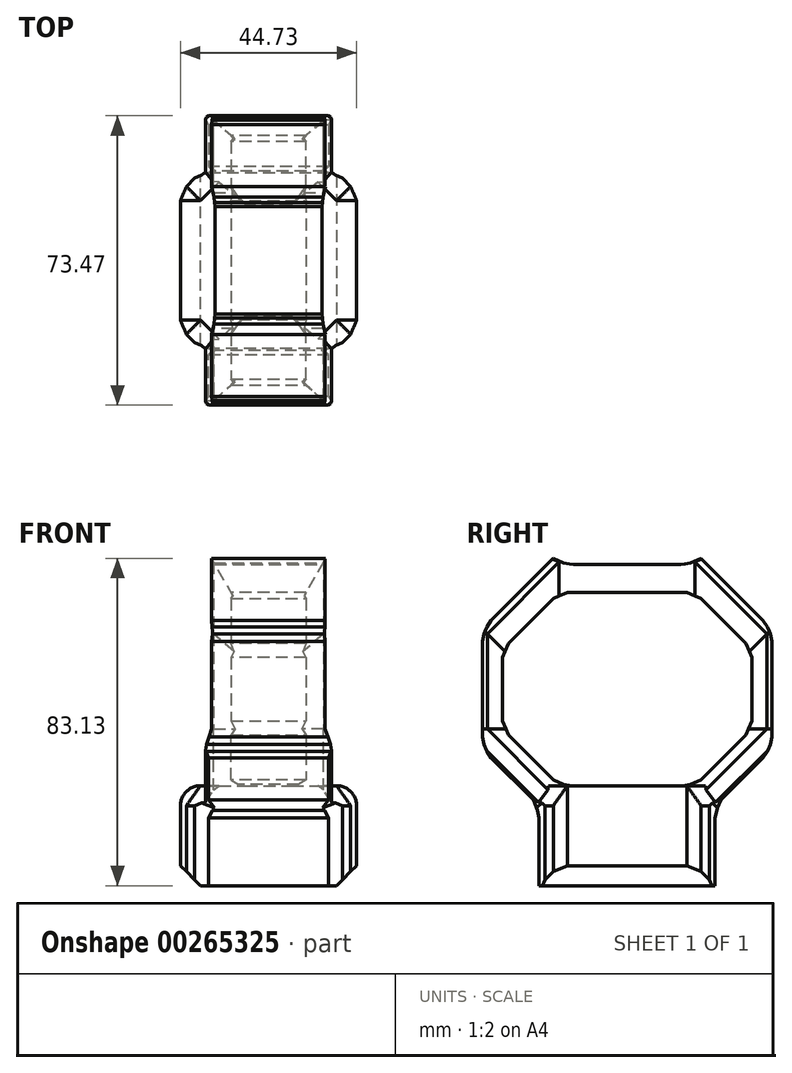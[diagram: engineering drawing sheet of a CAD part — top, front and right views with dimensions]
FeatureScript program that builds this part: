
annotation { "Feature Type Name" : "Feature", "Feature Type Description" : "" }
export const myFeature = defineFeature(function(context is Context, id is Id, definition is map)
    precondition{}
    {
        {
            var Q0;
            Q0=qCreatedBy(makeId("Top.planeOp"),FACE);
            var sketch = newSketch(context, id + "F0", { "sketchPlane" : qUnion([Q0])});
            skLineSegment(sketch, "E0", {"start": v(0, 0) * mm, "end": v(0, 44.73) * mm});
            skLineSegment(sketch, "E1", {"start": v(0, 44.73) * mm, "end": v(-44.73, 44.73) * mm});
            skLineSegment(sketch, "E2", {"start": v(-44.73, 44.73) * mm, "end": v(-44.73, 0) * mm});
            skLineSegment(sketch, "E3", {"start": v(-44.73, 0) * mm, "end": v(0, 0) * mm});
            skSolve(sketch);
        }
        {
            var Q0;
            Q0=makeQuery(id+"F0.imprint","IMPRINT",FACE,{"disambiguationData":[TD([[makeQuery(id+"F0.imprint","IMPRINT",EDGE,{"derivedFrom":sQuery(id+"F0.wireOp",EDGE,"E0")}),1.0]])]});
            extrude(context, id + "F1", {"entities" : qUnion([Q0]), "depth" : 25.4 * mm});
        }
        {
            var Q0;
            Q0=makeQuery(id+"F1.opExtrude","CAP_EDGE",EDGE,{"disambiguationData":[OSD([sQuery(id+"F0.wireOp",EDGE,"E3")])],"isStart":false});
            var Q1;
            Q1=makeQuery(id+"F1.opExtrude","SWEPT_EDGE",EDGE,{"disambiguationData":[OSD([sQuery(id+"F0.wireOp",EDGE,"E2"),sQuery(id+"F0.wireOp",EDGE,"E3")])]});
            var Q2;
            Q2=makeQuery(id+"F1.opExtrude","SWEPT_EDGE",EDGE,{"disambiguationData":[OSD([sQuery(id+"F0.wireOp",EDGE,"E0"),sQuery(id+"F0.wireOp",EDGE,"E3")])]});
            var Q3;
            Q3=makeQuery(id+"F1.opExtrude","CAP_EDGE",EDGE,{"disambiguationData":[OSD([sQuery(id+"F0.wireOp",EDGE,"E1")])],"isStart":false});
            var Q4;
            Q4=makeQuery(id+"F1.opExtrude","SWEPT_EDGE",EDGE,{"disambiguationData":[OSD([sQuery(id+"F0.wireOp",EDGE,"E1"),sQuery(id+"F0.wireOp",EDGE,"E2")])]});
            var Q5;
            Q5=makeQuery(id+"F1.opExtrude","SWEPT_EDGE",EDGE,{"disambiguationData":[OSD([sQuery(id+"F0.wireOp",EDGE,"E0"),sQuery(id+"F0.wireOp",EDGE,"E1")])]});
            chamfer(context, id + "F2", {"entities" : qUnion([Q0, Q1, Q2, Q3, Q4, Q5]), "width" : 5.08 * mm, "tangentPropagation" : true});
        }
        {
            var Q0;
            {var subQ0=sQuery(id+"F0.wireOp",EDGE,"E3");Q0=makeQuery(id+"F2.opChamfer","BLEND_EDGE",EDGE,{"blendedFrom":[makeQuery(id+"F1.opExtrude","SWEPT_EDGE",EDGE,{"disambiguationData":[OSD([sQuery(id+"F0.wireOp",EDGE,"E2"),subQ0])]}),makeQuery(id+"F1.opExtrude","SWEPT_FACE",FACE,{"disambiguationData":[OSD([subQ0])]})],"blendedInto":[makeQuery(id+"F1.opExtrude","SWEPT_FACE",FACE,{"disambiguationData":[OSD([subQ0])]})]});}
            var Q1;
            {var subQ0=sQuery(id+"F0.wireOp",EDGE,"E3");Q1=makeQuery(id+"F2.opChamfer","BLEND_EDGE",EDGE,{"blendedFrom":[makeQuery(id+"F1.opExtrude","SWEPT_EDGE",EDGE,{"disambiguationData":[OSD([sQuery(id+"F0.wireOp",EDGE,"E0"),subQ0])]}),makeQuery(id+"F1.opExtrude","SWEPT_FACE",FACE,{"disambiguationData":[OSD([subQ0])]})],"blendedInto":[makeQuery(id+"F1.opExtrude","SWEPT_FACE",FACE,{"disambiguationData":[OSD([subQ0])]})]});}
            var Q2;
            {var subQ0=sQuery(id+"F0.wireOp",EDGE,"E1");Q2=makeQuery(id+"F2.opChamfer","BLEND_EDGE",EDGE,{"blendedFrom":[makeQuery(id+"F1.opExtrude","SWEPT_EDGE",EDGE,{"disambiguationData":[OSD([sQuery(id+"F0.wireOp",EDGE,"E0"),subQ0])]}),makeQuery(id+"F1.opExtrude","SWEPT_FACE",FACE,{"disambiguationData":[OSD([subQ0])]})],"blendedInto":[makeQuery(id+"F1.opExtrude","SWEPT_FACE",FACE,{"disambiguationData":[OSD([subQ0])]})]});}
            var Q3;
            {var subQ0=sQuery(id+"F0.wireOp",EDGE,"E1");Q3=makeQuery(id+"F2.opChamfer","BLEND_EDGE",EDGE,{"blendedFrom":[makeQuery(id+"F1.opExtrude","SWEPT_EDGE",EDGE,{"disambiguationData":[OSD([subQ0,sQuery(id+"F0.wireOp",EDGE,"E2")])]}),makeQuery(id+"F1.opExtrude","SWEPT_FACE",FACE,{"disambiguationData":[OSD([subQ0])]})],"blendedInto":[makeQuery(id+"F1.opExtrude","SWEPT_FACE",FACE,{"disambiguationData":[OSD([subQ0])]})]});}
            chamfer(context, id + "F3", {"entities" : qUnion([Q0, Q1, Q2, Q3]), "width" : 5.08 * mm, "tangentPropagation" : true});
        }
        {
            var Q0;
            Q0=makeQuery(id+"F2.opChamfer","BLEND_FACE",FACE,{"disambiguationData":[OSD([sQuery(id+"F0.wireOp",EDGE,"E3")])]});
            extrude(context, id + "F4", {"entities" : qUnion([Q0]), "operationType" : NewBodyOperationType.ADD, "depth" : 25.4 * mm});
        }
        {
            var Q0;
            Q0=makeQuery(id+"F2.opChamfer","BLEND_FACE",FACE,{"disambiguationData":[OSD([sQuery(id+"F0.wireOp",EDGE,"E1")])]});
            extrude(context, id + "F5", {"entities" : qUnion([Q0]), "operationType" : NewBodyOperationType.ADD, "depth" : 25.4 * mm});
        }
        {
            var Q0;
            {var subQ0=sQuery(id+"F0.wireOp",EDGE,"E2");var subQ1=sQuery(id+"F0.wireOp",EDGE,"E3");var subQ2=sQuery(id+"F0.wireOp",EDGE,"E1");var subQ3=sQuery(id+"F0.wireOp",EDGE,"E0");Q0=makeQuery(id+"F5.opExtrude","SWEPT_EDGE",EDGE,{"disambiguationData":[OSD([subQ3,subQ2,subQ0,subQ1]),TDD([makeQuery(id+"F2.opChamfer","BLEND_VERTEX",VERTEX,{"blendedFrom":[makeQuery(id+"F1.opExtrude","SWEPT_EDGE",EDGE,{"disambiguationData":[OSD([subQ2,subQ0])]}),makeQuery(id+"F1.opExtrude","CAP_EDGE",EDGE,{"disambiguationData":[OSD([subQ2])],"isStart":false}),makeQuery(id+"F1.opExtrude","CAP_FACE",FACE,{"disambiguationData":[OSD([subQ3,subQ2,subQ0,subQ1])],"isStart":false}),makeQuery(id+"F1.opExtrude","SWEPT_FACE",FACE,{"disambiguationData":[OSD([subQ0])]})],"blendedInto":[makeQuery(id+"F1.opExtrude","CAP_FACE",FACE,{"disambiguationData":[OSD([subQ3,subQ2,subQ0,subQ1])],"isStart":false}),makeQuery(id+"F1.opExtrude","SWEPT_FACE",FACE,{"disambiguationData":[OSD([subQ0])]})]})])]});}
            var Q1;
            {var subQ0=sQuery(id+"F0.wireOp",EDGE,"E3");var subQ1=sQuery(id+"F0.wireOp",EDGE,"E2");var subQ2=sQuery(id+"F0.wireOp",EDGE,"E1");var subQ3=sQuery(id+"F0.wireOp",EDGE,"E0");Q1=makeQuery(id+"F5.opExtrude","SWEPT_EDGE",EDGE,{"disambiguationData":[OSD([subQ3,subQ2,subQ1,subQ0]),TDD([makeQuery(id+"F2.opChamfer","BLEND_VERTEX",VERTEX,{"blendedFrom":[makeQuery(id+"F1.opExtrude","SWEPT_EDGE",EDGE,{"disambiguationData":[OSD([subQ3,subQ2])]}),makeQuery(id+"F1.opExtrude","CAP_EDGE",EDGE,{"disambiguationData":[OSD([subQ2])],"isStart":false}),makeQuery(id+"F1.opExtrude","SWEPT_FACE",FACE,{"disambiguationData":[OSD([subQ3])]}),makeQuery(id+"F1.opExtrude","CAP_FACE",FACE,{"disambiguationData":[OSD([subQ3,subQ2,subQ1,subQ0])],"isStart":false})],"blendedInto":[makeQuery(id+"F1.opExtrude","SWEPT_FACE",FACE,{"disambiguationData":[OSD([subQ3])]}),makeQuery(id+"F1.opExtrude","CAP_FACE",FACE,{"disambiguationData":[OSD([subQ3,subQ2,subQ1,subQ0])],"isStart":false})]})])]});}
            var Q2;
            {var subQ0=sQuery(id+"F0.wireOp",EDGE,"E3");var subQ1=sQuery(id+"F0.wireOp",EDGE,"E2");var subQ2=sQuery(id+"F0.wireOp",EDGE,"E1");var subQ3=sQuery(id+"F0.wireOp",EDGE,"E0");Q2=makeQuery(id+"F4.opExtrude","SWEPT_EDGE",EDGE,{"disambiguationData":[OSD([subQ3,subQ2,subQ1,subQ0]),TDD([makeQuery(id+"F2.opChamfer","BLEND_VERTEX",VERTEX,{"blendedFrom":[makeQuery(id+"F1.opExtrude","SWEPT_EDGE",EDGE,{"disambiguationData":[OSD([subQ3,subQ0])]}),makeQuery(id+"F1.opExtrude","CAP_EDGE",EDGE,{"disambiguationData":[OSD([subQ0])],"isStart":false}),makeQuery(id+"F1.opExtrude","SWEPT_FACE",FACE,{"disambiguationData":[OSD([subQ3])]}),makeQuery(id+"F1.opExtrude","CAP_FACE",FACE,{"disambiguationData":[OSD([subQ3,subQ2,subQ1,subQ0])],"isStart":false})],"blendedInto":[makeQuery(id+"F1.opExtrude","SWEPT_FACE",FACE,{"disambiguationData":[OSD([subQ3])]}),makeQuery(id+"F1.opExtrude","CAP_FACE",FACE,{"disambiguationData":[OSD([subQ3,subQ2,subQ1,subQ0])],"isStart":false})]})])]});}
            var Q3;
            {var subQ0=sQuery(id+"F0.wireOp",EDGE,"E2");var subQ1=sQuery(id+"F0.wireOp",EDGE,"E3");var subQ2=sQuery(id+"F0.wireOp",EDGE,"E1");var subQ3=sQuery(id+"F0.wireOp",EDGE,"E0");Q3=makeQuery(id+"F4.opExtrude","SWEPT_EDGE",EDGE,{"disambiguationData":[OSD([subQ3,subQ2,subQ0,subQ1]),TDD([makeQuery(id+"F2.opChamfer","BLEND_VERTEX",VERTEX,{"blendedFrom":[makeQuery(id+"F1.opExtrude","SWEPT_EDGE",EDGE,{"disambiguationData":[OSD([subQ0,subQ1])]}),makeQuery(id+"F1.opExtrude","CAP_EDGE",EDGE,{"disambiguationData":[OSD([subQ1])],"isStart":false}),makeQuery(id+"F1.opExtrude","CAP_FACE",FACE,{"disambiguationData":[OSD([subQ3,subQ2,subQ0,subQ1])],"isStart":false}),makeQuery(id+"F1.opExtrude","SWEPT_FACE",FACE,{"disambiguationData":[OSD([subQ0])]})],"blendedInto":[makeQuery(id+"F1.opExtrude","CAP_FACE",FACE,{"disambiguationData":[OSD([subQ3,subQ2,subQ0,subQ1])],"isStart":false}),makeQuery(id+"F1.opExtrude","SWEPT_FACE",FACE,{"disambiguationData":[OSD([subQ0])]})]})])]});}
            chamfer(context, id + "F6", {"entities" : qUnion([Q0, Q1, Q2, Q3]), "width" : 5.08 * mm, "tangentPropagation" : true});
        }
        {
            var Q0;
            {var subQ0=sQuery(id+"F0.wireOp",EDGE,"E3");var subQ1=sQuery(id+"F0.wireOp",EDGE,"E2");var subQ2=sQuery(id+"F0.wireOp",EDGE,"E1");var subQ3=sQuery(id+"F0.wireOp",EDGE,"E0");Q0=makeQuery(id+"F6.opChamfer","BLEND_EDGE",EDGE,{"blendedFrom":[makeQuery(id+"F5.opExtrude","SWEPT_EDGE",EDGE,{"disambiguationData":[OSD([subQ3,subQ2,subQ1,subQ0]),TDD([makeQuery(id+"F2.opChamfer","BLEND_VERTEX",VERTEX,{"blendedFrom":[makeQuery(id+"F1.opExtrude","SWEPT_EDGE",EDGE,{"disambiguationData":[OSD([subQ3,subQ2])]}),makeQuery(id+"F1.opExtrude","CAP_EDGE",EDGE,{"disambiguationData":[OSD([subQ2])],"isStart":false}),makeQuery(id+"F1.opExtrude","SWEPT_FACE",FACE,{"disambiguationData":[OSD([subQ3])]}),makeQuery(id+"F1.opExtrude","CAP_FACE",FACE,{"disambiguationData":[OSD([subQ3,subQ2,subQ1,subQ0])],"isStart":false})],"blendedInto":[makeQuery(id+"F1.opExtrude","SWEPT_FACE",FACE,{"disambiguationData":[OSD([subQ3])]}),makeQuery(id+"F1.opExtrude","CAP_FACE",FACE,{"disambiguationData":[OSD([subQ3,subQ2,subQ1,subQ0])],"isStart":false})]})])]}),makeQuery(id+"F5.opExtrude","SWEPT_FACE",FACE,{"disambiguationData":[OSD([subQ3,subQ2,subQ1,subQ0])]})],"blendedInto":[makeQuery(id+"F5.opExtrude","SWEPT_FACE",FACE,{"disambiguationData":[OSD([subQ3,subQ2,subQ1,subQ0])]})]});}
            var Q1;
            {var subQ0=sQuery(id+"F0.wireOp",EDGE,"E3");var subQ1=sQuery(id+"F0.wireOp",EDGE,"E2");var subQ2=sQuery(id+"F0.wireOp",EDGE,"E1");var subQ3=sQuery(id+"F0.wireOp",EDGE,"E0");Q1=makeQuery(id+"F6.opChamfer","BLEND_EDGE",EDGE,{"blendedFrom":[makeQuery(id+"F5.opExtrude","SWEPT_EDGE",EDGE,{"disambiguationData":[OSD([subQ3,subQ2,subQ1,subQ0]),TDD([makeQuery(id+"F2.opChamfer","BLEND_VERTEX",VERTEX,{"blendedFrom":[makeQuery(id+"F1.opExtrude","SWEPT_EDGE",EDGE,{"disambiguationData":[OSD([subQ2,subQ1])]}),makeQuery(id+"F1.opExtrude","CAP_EDGE",EDGE,{"disambiguationData":[OSD([subQ2])],"isStart":false}),makeQuery(id+"F1.opExtrude","CAP_FACE",FACE,{"disambiguationData":[OSD([subQ3,subQ2,subQ1,subQ0])],"isStart":false}),makeQuery(id+"F1.opExtrude","SWEPT_FACE",FACE,{"disambiguationData":[OSD([subQ1])]})],"blendedInto":[makeQuery(id+"F1.opExtrude","CAP_FACE",FACE,{"disambiguationData":[OSD([subQ3,subQ2,subQ1,subQ0])],"isStart":false}),makeQuery(id+"F1.opExtrude","SWEPT_FACE",FACE,{"disambiguationData":[OSD([subQ1])]})]})])]}),makeQuery(id+"F5.opExtrude","SWEPT_FACE",FACE,{"disambiguationData":[OSD([subQ3,subQ2,subQ1,subQ0])]})],"blendedInto":[makeQuery(id+"F5.opExtrude","SWEPT_FACE",FACE,{"disambiguationData":[OSD([subQ3,subQ2,subQ1,subQ0])]})]});}
            var Q2;
            {var subQ0=sQuery(id+"F0.wireOp",EDGE,"E3");var subQ1=sQuery(id+"F0.wireOp",EDGE,"E2");var subQ2=sQuery(id+"F0.wireOp",EDGE,"E1");var subQ3=sQuery(id+"F0.wireOp",EDGE,"E0");Q2=makeQuery(id+"F6.opChamfer","BLEND_EDGE",EDGE,{"blendedFrom":[makeQuery(id+"F4.opExtrude","SWEPT_EDGE",EDGE,{"disambiguationData":[OSD([subQ3,subQ2,subQ1,subQ0]),TDD([makeQuery(id+"F2.opChamfer","BLEND_VERTEX",VERTEX,{"blendedFrom":[makeQuery(id+"F1.opExtrude","SWEPT_EDGE",EDGE,{"disambiguationData":[OSD([subQ3,subQ0])]}),makeQuery(id+"F1.opExtrude","CAP_EDGE",EDGE,{"disambiguationData":[OSD([subQ0])],"isStart":false}),makeQuery(id+"F1.opExtrude","SWEPT_FACE",FACE,{"disambiguationData":[OSD([subQ3])]}),makeQuery(id+"F1.opExtrude","CAP_FACE",FACE,{"disambiguationData":[OSD([subQ3,subQ2,subQ1,subQ0])],"isStart":false})],"blendedInto":[makeQuery(id+"F1.opExtrude","SWEPT_FACE",FACE,{"disambiguationData":[OSD([subQ3])]}),makeQuery(id+"F1.opExtrude","CAP_FACE",FACE,{"disambiguationData":[OSD([subQ3,subQ2,subQ1,subQ0])],"isStart":false})]})])]}),makeQuery(id+"F4.opExtrude","SWEPT_FACE",FACE,{"disambiguationData":[OSD([subQ3,subQ2,subQ1,subQ0])]})],"blendedInto":[makeQuery(id+"F4.opExtrude","SWEPT_FACE",FACE,{"disambiguationData":[OSD([subQ3,subQ2,subQ1,subQ0])]})]});}
            var Q3;
            {var subQ0=sQuery(id+"F0.wireOp",EDGE,"E3");var subQ1=sQuery(id+"F0.wireOp",EDGE,"E2");var subQ2=sQuery(id+"F0.wireOp",EDGE,"E1");var subQ3=sQuery(id+"F0.wireOp",EDGE,"E0");Q3=makeQuery(id+"F6.opChamfer","BLEND_EDGE",EDGE,{"blendedFrom":[makeQuery(id+"F4.opExtrude","SWEPT_EDGE",EDGE,{"disambiguationData":[OSD([subQ3,subQ2,subQ1,subQ0]),TDD([makeQuery(id+"F2.opChamfer","BLEND_VERTEX",VERTEX,{"blendedFrom":[makeQuery(id+"F1.opExtrude","SWEPT_EDGE",EDGE,{"disambiguationData":[OSD([subQ1,subQ0])]}),makeQuery(id+"F1.opExtrude","CAP_EDGE",EDGE,{"disambiguationData":[OSD([subQ0])],"isStart":false}),makeQuery(id+"F1.opExtrude","CAP_FACE",FACE,{"disambiguationData":[OSD([subQ3,subQ2,subQ1,subQ0])],"isStart":false}),makeQuery(id+"F1.opExtrude","SWEPT_FACE",FACE,{"disambiguationData":[OSD([subQ1])]})],"blendedInto":[makeQuery(id+"F1.opExtrude","CAP_FACE",FACE,{"disambiguationData":[OSD([subQ3,subQ2,subQ1,subQ0])],"isStart":false}),makeQuery(id+"F1.opExtrude","SWEPT_FACE",FACE,{"disambiguationData":[OSD([subQ1])]})]})])]}),makeQuery(id+"F4.opExtrude","SWEPT_FACE",FACE,{"disambiguationData":[OSD([subQ3,subQ2,subQ1,subQ0])]})],"blendedInto":[makeQuery(id+"F4.opExtrude","SWEPT_FACE",FACE,{"disambiguationData":[OSD([subQ3,subQ2,subQ1,subQ0])]})]});}
            chamfer(context, id + "F7", {"entities" : qUnion([Q0, Q1, Q2, Q3]), "width" : 5.08 * mm, "tangentPropagation" : true});
        }
        {
            var Q0;
            {var subQ0=sQuery(id+"F0.wireOp",EDGE,"E3");var subQ1=sQuery(id+"F0.wireOp",EDGE,"E2");var subQ2=sQuery(id+"F0.wireOp",EDGE,"E1");var subQ3=sQuery(id+"F0.wireOp",EDGE,"E0");Q0=makeQuery(id+"F5.boolean.opBoolean","MERGE",EDGE,{"derivedFrom":[makeQuery(id+"F2.opChamfer","BLEND_EDGE",EDGE,{"blendedFrom":[makeQuery(id+"F1.opExtrude","CAP_EDGE",EDGE,{"disambiguationData":[OSD([subQ2])],"isStart":false}),makeQuery(id+"F1.opExtrude","CAP_FACE",FACE,{"disambiguationData":[OSD([subQ3,subQ2,subQ1,subQ0])],"isStart":false})],"blendedInto":[makeQuery(id+"F1.opExtrude","CAP_FACE",FACE,{"disambiguationData":[OSD([subQ3,subQ2,subQ1,subQ0])],"isStart":false})]}),makeQuery(id+"F5.opExtrude","CAP_EDGE",EDGE,{"disambiguationData":[OSD([subQ3,subQ2,subQ1,subQ0])],"isStart":true})]});}
            var Q1;
            {var subQ0=sQuery(id+"F0.wireOp",EDGE,"E3");var subQ1=sQuery(id+"F0.wireOp",EDGE,"E2");var subQ2=sQuery(id+"F0.wireOp",EDGE,"E1");var subQ3=sQuery(id+"F0.wireOp",EDGE,"E0");Q1=makeQuery(id+"F4.boolean.opBoolean","MERGE",EDGE,{"derivedFrom":[makeQuery(id+"F2.opChamfer","BLEND_EDGE",EDGE,{"blendedFrom":[makeQuery(id+"F1.opExtrude","CAP_EDGE",EDGE,{"disambiguationData":[OSD([subQ0])],"isStart":false}),makeQuery(id+"F1.opExtrude","CAP_FACE",FACE,{"disambiguationData":[OSD([subQ3,subQ2,subQ1,subQ0])],"isStart":false})],"blendedInto":[makeQuery(id+"F1.opExtrude","CAP_FACE",FACE,{"disambiguationData":[OSD([subQ3,subQ2,subQ1,subQ0])],"isStart":false})]}),makeQuery(id+"F4.opExtrude","CAP_EDGE",EDGE,{"disambiguationData":[OSD([subQ3,subQ2,subQ1,subQ0])],"isStart":true})]});}
            chamfer(context, id + "F8", {"entities" : qUnion([Q0, Q1]), "width" : 5.08 * mm, "tangentPropagation" : true});
        }
        {
            var Q0;
            Q0=makeQuery(id+"F5.opExtrude","CAP_EDGE",EDGE,{"disambiguationData":[OSD([sQuery(id+"F0.wireOp",EDGE,"E0"),sQuery(id+"F0.wireOp",EDGE,"E1"),sQuery(id+"F0.wireOp",EDGE,"E2"),sQuery(id+"F0.wireOp",EDGE,"E3")])],"isStart":false});
            chamfer(context, id + "F9", {"entities" : qUnion([Q0]), "width" : 5.08 * mm, "tangentPropagation" : true});
        }
        {
            var Q0;
            Q0=makeQuery(id+"F5.opExtrude","CAP_EDGE",EDGE,{"disambiguationData":[OSD([sQuery(id+"F0.wireOp",EDGE,"E1")])],"isStart":false});
            var Q1;
            Q1=makeQuery(id+"F4.opExtrude","CAP_EDGE",EDGE,{"disambiguationData":[OSD([sQuery(id+"F0.wireOp",EDGE,"E0"),sQuery(id+"F0.wireOp",EDGE,"E1"),sQuery(id+"F0.wireOp",EDGE,"E2"),sQuery(id+"F0.wireOp",EDGE,"E3")])],"isStart":false});
            chamfer(context, id + "F10", {"entities" : qUnion([Q0, Q1]), "width" : 5.08 * mm, "tangentPropagation" : true});
        }
        {
            var Q0;
            Q0=makeQuery(id+"F4.opExtrude","CAP_EDGE",EDGE,{"disambiguationData":[OSD([sQuery(id+"F0.wireOp",EDGE,"E3")])],"isStart":false});
            chamfer(context, id + "F11", {"entities" : qUnion([Q0]), "width" : 5.08 * mm, "tangentPropagation" : true});
        }
        {
            var Q0;
            Q0=makeQuery(id+"F9.opChamfer","BLEND_FACE",FACE,{"disambiguationData":[OSD([sQuery(id+"F0.wireOp",EDGE,"E0"),sQuery(id+"F0.wireOp",EDGE,"E1"),sQuery(id+"F0.wireOp",EDGE,"E2"),sQuery(id+"F0.wireOp",EDGE,"E3")])]});
            extrude(context, id + "F12", {"entities" : qUnion([Q0]), "operationType" : NewBodyOperationType.ADD, "depth" : 25.4 * mm});
        }
        {
            var Q0;
            Q0=makeQuery(id+"F10.opChamfer","BLEND_FACE",FACE,{"disambiguationData":[OSD([sQuery(id+"F0.wireOp",EDGE,"E0"),sQuery(id+"F0.wireOp",EDGE,"E1"),sQuery(id+"F0.wireOp",EDGE,"E2"),sQuery(id+"F0.wireOp",EDGE,"E3")])]});
            extrude(context, id + "F13", {"entities" : qUnion([Q0]), "operationType" : NewBodyOperationType.ADD, "depth" : 25.4 * mm});
        }
        {
            var Q0;
            {var subQ0=sQuery(id+"F0.wireOp",EDGE,"E3");var subQ1=sQuery(id+"F0.wireOp",EDGE,"E2");var subQ2=sQuery(id+"F0.wireOp",EDGE,"E1");var subQ3=sQuery(id+"F0.wireOp",EDGE,"E0");Q0=makeQuery(id+"F12.opExtrude","CAP_EDGE",EDGE,{"disambiguationData":[OSD([subQ3,subQ2,subQ1,subQ0]),TDD([makeQuery(id+"F9.opChamfer","BLEND_EDGE",EDGE,{"blendedFrom":[makeQuery(id+"F5.opExtrude","CAP_EDGE",EDGE,{"disambiguationData":[OSD([subQ3,subQ2,subQ1,subQ0])],"isStart":false}),makeQuery(id+"F5.opExtrude","SWEPT_FACE",FACE,{"disambiguationData":[OSD([subQ3,subQ2,subQ1,subQ0])]})],"blendedInto":[makeQuery(id+"F5.opExtrude","SWEPT_FACE",FACE,{"disambiguationData":[OSD([subQ3,subQ2,subQ1,subQ0])]})]})])],"isStart":false});}
            var Q1;
            {var subQ0=sQuery(id+"F0.wireOp",EDGE,"E3");var subQ1=sQuery(id+"F0.wireOp",EDGE,"E2");var subQ2=sQuery(id+"F0.wireOp",EDGE,"E1");var subQ3=sQuery(id+"F0.wireOp",EDGE,"E0");Q1=makeQuery(id+"F13.opExtrude","CAP_EDGE",EDGE,{"disambiguationData":[OSD([subQ3,subQ2,subQ1,subQ0]),TDD([makeQuery(id+"F10.opChamfer","BLEND_EDGE",EDGE,{"blendedFrom":[makeQuery(id+"F4.opExtrude","CAP_EDGE",EDGE,{"disambiguationData":[OSD([subQ3,subQ2,subQ1,subQ0])],"isStart":false}),makeQuery(id+"F4.opExtrude","SWEPT_FACE",FACE,{"disambiguationData":[OSD([subQ3,subQ2,subQ1,subQ0])]})],"blendedInto":[makeQuery(id+"F4.opExtrude","SWEPT_FACE",FACE,{"disambiguationData":[OSD([subQ3,subQ2,subQ1,subQ0])]})]})])],"isStart":false});}
            chamfer(context, id + "F14", {"entities" : qUnion([Q0, Q1]), "width" : 5.08 * mm, "tangentPropagation" : true});
        }
        {
            var Q0;
            {var subQ0=sQuery(id+"F0.wireOp",EDGE,"E3");var subQ1=sQuery(id+"F0.wireOp",EDGE,"E2");var subQ2=sQuery(id+"F0.wireOp",EDGE,"E1");var subQ3=sQuery(id+"F0.wireOp",EDGE,"E0");Q0=makeQuery(id+"F14.opChamfer","BLEND_FACE",FACE,{"disambiguationData":[OSD([subQ3,subQ2,subQ1,subQ0]),TDD([makeQuery(id+"F13.opExtrude","CAP_EDGE",EDGE,{"disambiguationData":[OSD([subQ3,subQ2,subQ1,subQ0]),TDD([makeQuery(id+"F10.opChamfer","BLEND_EDGE",EDGE,{"blendedFrom":[makeQuery(id+"F4.opExtrude","CAP_EDGE",EDGE,{"disambiguationData":[OSD([subQ3,subQ2,subQ1,subQ0])],"isStart":false}),makeQuery(id+"F4.opExtrude","SWEPT_FACE",FACE,{"disambiguationData":[OSD([subQ3,subQ2,subQ1,subQ0])]})],"blendedInto":[makeQuery(id+"F4.opExtrude","SWEPT_FACE",FACE,{"disambiguationData":[OSD([subQ3,subQ2,subQ1,subQ0])]})]})])],"isStart":false})])]});}
            extrude(context, id + "F15", {"entities" : qUnion([Q0]), "operationType" : NewBodyOperationType.ADD, "depth" : 25.4 * mm});
        }
        {
            var Q0;
            {var subQ0=sQuery(id+"F0.wireOp",EDGE,"E3");var subQ1=sQuery(id+"F0.wireOp",EDGE,"E2");var subQ2=sQuery(id+"F0.wireOp",EDGE,"E1");var subQ3=sQuery(id+"F0.wireOp",EDGE,"E0");Q0=makeQuery(id+"F14.opChamfer","BLEND_FACE",FACE,{"disambiguationData":[OSD([subQ3,subQ2,subQ1,subQ0]),TDD([makeQuery(id+"F12.opExtrude","CAP_EDGE",EDGE,{"disambiguationData":[OSD([subQ3,subQ2,subQ1,subQ0]),TDD([makeQuery(id+"F9.opChamfer","BLEND_EDGE",EDGE,{"blendedFrom":[makeQuery(id+"F5.opExtrude","CAP_EDGE",EDGE,{"disambiguationData":[OSD([subQ3,subQ2,subQ1,subQ0])],"isStart":false}),makeQuery(id+"F5.opExtrude","SWEPT_FACE",FACE,{"disambiguationData":[OSD([subQ3,subQ2,subQ1,subQ0])]})],"blendedInto":[makeQuery(id+"F5.opExtrude","SWEPT_FACE",FACE,{"disambiguationData":[OSD([subQ3,subQ2,subQ1,subQ0])]})]})])],"isStart":false})])]});}
            extrude(context, id + "F16", {"entities" : qUnion([Q0]), "operationType" : NewBodyOperationType.ADD, "depth" : 25.4 * mm});
        }
        {
            var Q0;
            {var subQ0=sQuery(id+"F0.wireOp",EDGE,"E3");var subQ1=sQuery(id+"F0.wireOp",EDGE,"E2");var subQ2=sQuery(id+"F0.wireOp",EDGE,"E1");var subQ3=sQuery(id+"F0.wireOp",EDGE,"E0");var subQ4=makeQuery(id+"F9.opChamfer","BLEND_EDGE",EDGE,{"blendedFrom":[makeQuery(id+"F5.opExtrude","CAP_EDGE",EDGE,{"disambiguationData":[OSD([subQ3,subQ2,subQ1,subQ0])],"isStart":false}),makeQuery(id+"F5.opExtrude","SWEPT_FACE",FACE,{"disambiguationData":[OSD([subQ3,subQ2,subQ1,subQ0])]})],"blendedInto":[makeQuery(id+"F5.opExtrude","SWEPT_FACE",FACE,{"disambiguationData":[OSD([subQ3,subQ2,subQ1,subQ0])]})]});Q0=makeQuery(id+"F16.opExtrude","CAP_EDGE",EDGE,{"disambiguationData":[OSD([subQ3,subQ2,subQ1,subQ0]),TDD([makeQuery(id+"F14.opChamfer","BLEND_EDGE",EDGE,{"blendedFrom":[makeQuery(id+"F12.opExtrude","CAP_EDGE",EDGE,{"disambiguationData":[OSD([subQ3,subQ2,subQ1,subQ0]),TDD([subQ4])],"isStart":false}),makeQuery(id+"F12.opExtrude","SWEPT_FACE",FACE,{"disambiguationData":[OSD([subQ3,subQ2,subQ1,subQ0]),TDD([subQ4])]})],"blendedInto":[makeQuery(id+"F12.opExtrude","SWEPT_FACE",FACE,{"disambiguationData":[OSD([subQ3,subQ2,subQ1,subQ0]),TDD([subQ4])]})]})])],"isStart":false});}
            var Q1;
            {var subQ0=sQuery(id+"F0.wireOp",EDGE,"E3");var subQ1=sQuery(id+"F0.wireOp",EDGE,"E2");var subQ2=sQuery(id+"F0.wireOp",EDGE,"E1");var subQ3=sQuery(id+"F0.wireOp",EDGE,"E0");var subQ4=makeQuery(id+"F10.opChamfer","BLEND_EDGE",EDGE,{"blendedFrom":[makeQuery(id+"F4.opExtrude","CAP_EDGE",EDGE,{"disambiguationData":[OSD([subQ3,subQ2,subQ1,subQ0])],"isStart":false}),makeQuery(id+"F4.opExtrude","SWEPT_FACE",FACE,{"disambiguationData":[OSD([subQ3,subQ2,subQ1,subQ0])]})],"blendedInto":[makeQuery(id+"F4.opExtrude","SWEPT_FACE",FACE,{"disambiguationData":[OSD([subQ3,subQ2,subQ1,subQ0])]})]});Q1=makeQuery(id+"F15.opExtrude","CAP_EDGE",EDGE,{"disambiguationData":[OSD([subQ3,subQ2,subQ1,subQ0]),TDD([makeQuery(id+"F14.opChamfer","BLEND_EDGE",EDGE,{"blendedFrom":[makeQuery(id+"F13.opExtrude","CAP_EDGE",EDGE,{"disambiguationData":[OSD([subQ3,subQ2,subQ1,subQ0]),TDD([subQ4])],"isStart":false}),makeQuery(id+"F13.opExtrude","SWEPT_FACE",FACE,{"disambiguationData":[OSD([subQ3,subQ2,subQ1,subQ0]),TDD([subQ4])]})],"blendedInto":[makeQuery(id+"F13.opExtrude","SWEPT_FACE",FACE,{"disambiguationData":[OSD([subQ3,subQ2,subQ1,subQ0]),TDD([subQ4])]})]})])],"isStart":false});}
            chamfer(context, id + "F17", {"entities" : qUnion([Q0, Q1]), "width" : 5.08 * mm, "tangentPropagation" : true});
        }
        {
            var Q0;
            {var subQ0=sQuery(id+"F0.wireOp",EDGE,"E3");var subQ1=sQuery(id+"F0.wireOp",EDGE,"E2");var subQ2=sQuery(id+"F0.wireOp",EDGE,"E1");var subQ3=sQuery(id+"F0.wireOp",EDGE,"E0");var subQ4=makeQuery(id+"F10.opChamfer","BLEND_EDGE",EDGE,{"blendedFrom":[makeQuery(id+"F4.opExtrude","CAP_EDGE",EDGE,{"disambiguationData":[OSD([subQ3,subQ2,subQ1,subQ0])],"isStart":false}),makeQuery(id+"F4.opExtrude","SWEPT_FACE",FACE,{"disambiguationData":[OSD([subQ3,subQ2,subQ1,subQ0])]})],"blendedInto":[makeQuery(id+"F4.opExtrude","SWEPT_FACE",FACE,{"disambiguationData":[OSD([subQ3,subQ2,subQ1,subQ0])]})]});Q0=makeQuery(id+"F17.opChamfer","BLEND_FACE",FACE,{"disambiguationData":[OSD([subQ3,subQ2,subQ1,subQ0]),TDD([makeQuery(id+"F15.opExtrude","CAP_EDGE",EDGE,{"disambiguationData":[OSD([subQ3,subQ2,subQ1,subQ0]),TDD([makeQuery(id+"F14.opChamfer","BLEND_EDGE",EDGE,{"blendedFrom":[makeQuery(id+"F13.opExtrude","CAP_EDGE",EDGE,{"disambiguationData":[OSD([subQ3,subQ2,subQ1,subQ0]),TDD([subQ4])],"isStart":false}),makeQuery(id+"F13.opExtrude","SWEPT_FACE",FACE,{"disambiguationData":[OSD([subQ3,subQ2,subQ1,subQ0]),TDD([subQ4])]})],"blendedInto":[makeQuery(id+"F13.opExtrude","SWEPT_FACE",FACE,{"disambiguationData":[OSD([subQ3,subQ2,subQ1,subQ0]),TDD([subQ4])]})]})])],"isStart":false})])]});}
            extrude(context, id + "F18", {"entities" : qUnion([Q0]), "operationType" : NewBodyOperationType.ADD, "depth" : 25.4 * mm});
        }
        {
            var Q0;
            {var subQ0=sQuery(id+"F0.wireOp",EDGE,"E3");var subQ1=sQuery(id+"F0.wireOp",EDGE,"E2");var subQ2=sQuery(id+"F0.wireOp",EDGE,"E1");var subQ3=sQuery(id+"F0.wireOp",EDGE,"E0");var subQ4=makeQuery(id+"F9.opChamfer","BLEND_EDGE",EDGE,{"blendedFrom":[makeQuery(id+"F5.opExtrude","CAP_EDGE",EDGE,{"disambiguationData":[OSD([subQ3,subQ2,subQ1,subQ0])],"isStart":false}),makeQuery(id+"F5.opExtrude","SWEPT_FACE",FACE,{"disambiguationData":[OSD([subQ3,subQ2,subQ1,subQ0])]})],"blendedInto":[makeQuery(id+"F5.opExtrude","SWEPT_FACE",FACE,{"disambiguationData":[OSD([subQ3,subQ2,subQ1,subQ0])]})]});Q0=makeQuery(id+"F17.opChamfer","BLEND_FACE",FACE,{"disambiguationData":[OSD([subQ3,subQ2,subQ1,subQ0]),TDD([makeQuery(id+"F16.opExtrude","CAP_EDGE",EDGE,{"disambiguationData":[OSD([subQ3,subQ2,subQ1,subQ0]),TDD([makeQuery(id+"F14.opChamfer","BLEND_EDGE",EDGE,{"blendedFrom":[makeQuery(id+"F12.opExtrude","CAP_EDGE",EDGE,{"disambiguationData":[OSD([subQ3,subQ2,subQ1,subQ0]),TDD([subQ4])],"isStart":false}),makeQuery(id+"F12.opExtrude","SWEPT_FACE",FACE,{"disambiguationData":[OSD([subQ3,subQ2,subQ1,subQ0]),TDD([subQ4])]})],"blendedInto":[makeQuery(id+"F12.opExtrude","SWEPT_FACE",FACE,{"disambiguationData":[OSD([subQ3,subQ2,subQ1,subQ0]),TDD([subQ4])]})]})])],"isStart":false})])]});}
            extrude(context, id + "F19", {"entities" : qUnion([Q0]), "operationType" : NewBodyOperationType.ADD, "depth" : 25.4 * mm});
        }
        {
            var Q0;
            {var subQ0=sQuery(id+"F0.wireOp",EDGE,"E3");var subQ1=sQuery(id+"F0.wireOp",EDGE,"E2");var subQ2=sQuery(id+"F0.wireOp",EDGE,"E1");var subQ3=sQuery(id+"F0.wireOp",EDGE,"E0");var subQ4=makeQuery(id+"F9.opChamfer","BLEND_EDGE",EDGE,{"blendedFrom":[makeQuery(id+"F5.opExtrude","CAP_EDGE",EDGE,{"disambiguationData":[OSD([subQ3,subQ2,subQ1,subQ0])],"isStart":false}),makeQuery(id+"F5.opExtrude","SWEPT_FACE",FACE,{"disambiguationData":[OSD([subQ3,subQ2,subQ1,subQ0])]})],"blendedInto":[makeQuery(id+"F5.opExtrude","SWEPT_FACE",FACE,{"disambiguationData":[OSD([subQ3,subQ2,subQ1,subQ0])]})]});var subQ5=makeQuery(id+"F17.opChamfer","BLEND_EDGE",EDGE,{"blendedFrom":[makeQuery(id+"F16.opExtrude","CAP_EDGE",EDGE,{"disambiguationData":[OSD([subQ3,subQ2,subQ1,subQ0]),TDD([makeQuery(id+"F14.opChamfer","BLEND_EDGE",EDGE,{"blendedFrom":[makeQuery(id+"F12.opExtrude","CAP_EDGE",EDGE,{"disambiguationData":[OSD([subQ3,subQ2,subQ1,subQ0]),TDD([subQ4])],"isStart":false}),makeQuery(id+"F12.opExtrude","SWEPT_FACE",FACE,{"disambiguationData":[OSD([subQ3,subQ2,subQ1,subQ0]),TDD([subQ4])]})],"blendedInto":[makeQuery(id+"F12.opExtrude","SWEPT_FACE",FACE,{"disambiguationData":[OSD([subQ3,subQ2,subQ1,subQ0]),TDD([subQ4])]})]})])],"isStart":false}),makeQuery(id+"F16.opExtrude","CAP_FACE",FACE,{"disambiguationData":[OSD([subQ3,subQ2,subQ1,subQ0])],"isStart":false})],"blendedInto":[makeQuery(id+"F16.opExtrude","CAP_FACE",FACE,{"disambiguationData":[OSD([subQ3,subQ2,subQ1,subQ0])],"isStart":false})]});Q0=makeQuery(id+"F19.boolean.opBoolean","MERGE",EDGE,{"derivedFrom":[subQ5,makeQuery(id+"F19.opExtrude","CAP_EDGE",EDGE,{"disambiguationData":[OSD([subQ3,subQ2,subQ1,subQ0]),TDD([subQ5])],"isStart":true})]});}
            var Q1;
            {var subQ0=sQuery(id+"F0.wireOp",EDGE,"E3");var subQ1=sQuery(id+"F0.wireOp",EDGE,"E2");var subQ2=sQuery(id+"F0.wireOp",EDGE,"E1");var subQ3=sQuery(id+"F0.wireOp",EDGE,"E0");var subQ4=makeQuery(id+"F10.opChamfer","BLEND_EDGE",EDGE,{"blendedFrom":[makeQuery(id+"F4.opExtrude","CAP_EDGE",EDGE,{"disambiguationData":[OSD([subQ3,subQ2,subQ1,subQ0])],"isStart":false}),makeQuery(id+"F4.opExtrude","SWEPT_FACE",FACE,{"disambiguationData":[OSD([subQ3,subQ2,subQ1,subQ0])]})],"blendedInto":[makeQuery(id+"F4.opExtrude","SWEPT_FACE",FACE,{"disambiguationData":[OSD([subQ3,subQ2,subQ1,subQ0])]})]});var subQ5=makeQuery(id+"F17.opChamfer","BLEND_EDGE",EDGE,{"blendedFrom":[makeQuery(id+"F15.opExtrude","CAP_EDGE",EDGE,{"disambiguationData":[OSD([subQ3,subQ2,subQ1,subQ0]),TDD([makeQuery(id+"F14.opChamfer","BLEND_EDGE",EDGE,{"blendedFrom":[makeQuery(id+"F13.opExtrude","CAP_EDGE",EDGE,{"disambiguationData":[OSD([subQ3,subQ2,subQ1,subQ0]),TDD([subQ4])],"isStart":false}),makeQuery(id+"F13.opExtrude","SWEPT_FACE",FACE,{"disambiguationData":[OSD([subQ3,subQ2,subQ1,subQ0]),TDD([subQ4])]})],"blendedInto":[makeQuery(id+"F13.opExtrude","SWEPT_FACE",FACE,{"disambiguationData":[OSD([subQ3,subQ2,subQ1,subQ0]),TDD([subQ4])]})]})])],"isStart":false}),makeQuery(id+"F15.opExtrude","CAP_FACE",FACE,{"disambiguationData":[OSD([subQ3,subQ2,subQ1,subQ0])],"isStart":false})],"blendedInto":[makeQuery(id+"F15.opExtrude","CAP_FACE",FACE,{"disambiguationData":[OSD([subQ3,subQ2,subQ1,subQ0])],"isStart":false})]});Q1=makeQuery(id+"F18.boolean.opBoolean","MERGE",EDGE,{"derivedFrom":[subQ5,makeQuery(id+"F18.opExtrude","CAP_EDGE",EDGE,{"disambiguationData":[OSD([subQ3,subQ2,subQ1,subQ0]),TDD([subQ5])],"isStart":true})]});}
            chamfer(context, id + "F20", {"entities" : qUnion([Q0, Q1]), "width" : 5.08 * mm, "tangentPropagation" : true});
        }
        {
            var Q0;
            {var subQ0=sQuery(id+"F0.wireOp",EDGE,"E3");var subQ1=sQuery(id+"F0.wireOp",EDGE,"E2");var subQ2=sQuery(id+"F0.wireOp",EDGE,"E1");var subQ3=sQuery(id+"F0.wireOp",EDGE,"E0");var subQ4=makeQuery(id+"F9.opChamfer","BLEND_EDGE",EDGE,{"blendedFrom":[makeQuery(id+"F5.opExtrude","CAP_EDGE",EDGE,{"disambiguationData":[OSD([subQ3,subQ2,subQ1,subQ0])],"isStart":false}),makeQuery(id+"F5.opExtrude","SWEPT_FACE",FACE,{"disambiguationData":[OSD([subQ3,subQ2,subQ1,subQ0])]})],"blendedInto":[makeQuery(id+"F5.opExtrude","SWEPT_FACE",FACE,{"disambiguationData":[OSD([subQ3,subQ2,subQ1,subQ0])]})]});var subQ5=makeQuery(id+"F17.opChamfer","BLEND_EDGE",EDGE,{"blendedFrom":[makeQuery(id+"F16.opExtrude","CAP_EDGE",EDGE,{"disambiguationData":[OSD([subQ3,subQ2,subQ1,subQ0]),TDD([makeQuery(id+"F14.opChamfer","BLEND_EDGE",EDGE,{"blendedFrom":[makeQuery(id+"F12.opExtrude","CAP_EDGE",EDGE,{"disambiguationData":[OSD([subQ3,subQ2,subQ1,subQ0]),TDD([subQ4])],"isStart":false}),makeQuery(id+"F12.opExtrude","SWEPT_FACE",FACE,{"disambiguationData":[OSD([subQ3,subQ2,subQ1,subQ0]),TDD([subQ4])]})],"blendedInto":[makeQuery(id+"F12.opExtrude","SWEPT_FACE",FACE,{"disambiguationData":[OSD([subQ3,subQ2,subQ1,subQ0]),TDD([subQ4])]})]})])],"isStart":false}),makeQuery(id+"F16.opExtrude","CAP_FACE",FACE,{"disambiguationData":[OSD([subQ3,subQ2,subQ1,subQ0])],"isStart":false})],"blendedInto":[makeQuery(id+"F16.opExtrude","CAP_FACE",FACE,{"disambiguationData":[OSD([subQ3,subQ2,subQ1,subQ0])],"isStart":false})]});var subQ6=makeQuery(id+"F10.opChamfer","BLEND_EDGE",EDGE,{"blendedFrom":[makeQuery(id+"F4.opExtrude","CAP_EDGE",EDGE,{"disambiguationData":[OSD([subQ3,subQ2,subQ1,subQ0])],"isStart":false}),makeQuery(id+"F4.opExtrude","SWEPT_FACE",FACE,{"disambiguationData":[OSD([subQ3,subQ2,subQ1,subQ0])]})],"blendedInto":[makeQuery(id+"F4.opExtrude","SWEPT_FACE",FACE,{"disambiguationData":[OSD([subQ3,subQ2,subQ1,subQ0])]})]});Q0=makeQuery(id+"F20.opChamfer","BLEND_EDGE",EDGE,{"blendedFrom":[makeQuery(id+"F19.boolean.opBoolean","MERGE",EDGE,{"derivedFrom":[subQ5,makeQuery(id+"F19.opExtrude","CAP_EDGE",EDGE,{"disambiguationData":[OSD([subQ3,subQ2,subQ1,subQ0]),TDD([subQ5])],"isStart":true})]}),makeQuery(id+"F19.boolean.opBoolean","MERGE",FACE,{"derivedFrom":[makeQuery(id+"F18.opExtrude","SWEPT_FACE",FACE,{"disambiguationData":[OSD([subQ3,subQ2,subQ1,subQ0]),TDD([makeQuery(id+"F17.opChamfer","BLEND_EDGE",EDGE,{"blendedFrom":[makeQuery(id+"F15.opExtrude","CAP_EDGE",EDGE,{"disambiguationData":[OSD([subQ3,subQ2,subQ1,subQ0]),TDD([makeQuery(id+"F14.opChamfer","BLEND_EDGE",EDGE,{"blendedFrom":[makeQuery(id+"F13.opExtrude","CAP_EDGE",EDGE,{"disambiguationData":[OSD([subQ3,subQ2,subQ1,subQ0]),TDD([subQ6])],"isStart":false}),makeQuery(id+"F13.opExtrude","SWEPT_FACE",FACE,{"disambiguationData":[OSD([subQ3,subQ2,subQ1,subQ0]),TDD([subQ6])]})],"blendedInto":[makeQuery(id+"F13.opExtrude","SWEPT_FACE",FACE,{"disambiguationData":[OSD([subQ3,subQ2,subQ1,subQ0]),TDD([subQ6])]})]})])],"isStart":false}),makeQuery(id+"F15.opExtrude","CAP_FACE",FACE,{"disambiguationData":[OSD([subQ3,subQ2,subQ1,subQ0])],"isStart":false})],"blendedInto":[makeQuery(id+"F15.opExtrude","CAP_FACE",FACE,{"disambiguationData":[OSD([subQ3,subQ2,subQ1,subQ0])],"isStart":false})]})])]}),makeQuery(id+"F19.opExtrude","SWEPT_FACE",FACE,{"disambiguationData":[OSD([subQ3,subQ2,subQ1,subQ0]),TDD([subQ5])]})]})],"blendedInto":[makeQuery(id+"F19.boolean.opBoolean","MERGE",FACE,{"derivedFrom":[makeQuery(id+"F18.opExtrude","SWEPT_FACE",FACE,{"disambiguationData":[OSD([subQ3,subQ2,subQ1,subQ0]),TDD([makeQuery(id+"F17.opChamfer","BLEND_EDGE",EDGE,{"blendedFrom":[makeQuery(id+"F15.opExtrude","CAP_EDGE",EDGE,{"disambiguationData":[OSD([subQ3,subQ2,subQ1,subQ0]),TDD([makeQuery(id+"F14.opChamfer","BLEND_EDGE",EDGE,{"blendedFrom":[makeQuery(id+"F13.opExtrude","CAP_EDGE",EDGE,{"disambiguationData":[OSD([subQ3,subQ2,subQ1,subQ0]),TDD([subQ6])],"isStart":false}),makeQuery(id+"F13.opExtrude","SWEPT_FACE",FACE,{"disambiguationData":[OSD([subQ3,subQ2,subQ1,subQ0]),TDD([subQ6])]})],"blendedInto":[makeQuery(id+"F13.opExtrude","SWEPT_FACE",FACE,{"disambiguationData":[OSD([subQ3,subQ2,subQ1,subQ0]),TDD([subQ6])]})]})])],"isStart":false}),makeQuery(id+"F15.opExtrude","CAP_FACE",FACE,{"disambiguationData":[OSD([subQ3,subQ2,subQ1,subQ0])],"isStart":false})],"blendedInto":[makeQuery(id+"F15.opExtrude","CAP_FACE",FACE,{"disambiguationData":[OSD([subQ3,subQ2,subQ1,subQ0])],"isStart":false})]})])]}),makeQuery(id+"F19.opExtrude","SWEPT_FACE",FACE,{"disambiguationData":[OSD([subQ3,subQ2,subQ1,subQ0]),TDD([subQ5])]})]})]});}
            var Q1;
            {var subQ0=sQuery(id+"F0.wireOp",EDGE,"E3");var subQ1=sQuery(id+"F0.wireOp",EDGE,"E2");var subQ2=sQuery(id+"F0.wireOp",EDGE,"E1");var subQ3=sQuery(id+"F0.wireOp",EDGE,"E0");var subQ4=makeQuery(id+"F9.opChamfer","BLEND_EDGE",EDGE,{"blendedFrom":[makeQuery(id+"F5.opExtrude","CAP_EDGE",EDGE,{"disambiguationData":[OSD([subQ3,subQ2,subQ1,subQ0])],"isStart":false}),makeQuery(id+"F5.opExtrude","SWEPT_FACE",FACE,{"disambiguationData":[OSD([subQ3,subQ2,subQ1,subQ0])]})],"blendedInto":[makeQuery(id+"F5.opExtrude","SWEPT_FACE",FACE,{"disambiguationData":[OSD([subQ3,subQ2,subQ1,subQ0])]})]});var subQ5=makeQuery(id+"F10.opChamfer","BLEND_EDGE",EDGE,{"blendedFrom":[makeQuery(id+"F4.opExtrude","CAP_EDGE",EDGE,{"disambiguationData":[OSD([subQ3,subQ2,subQ1,subQ0])],"isStart":false}),makeQuery(id+"F4.opExtrude","SWEPT_FACE",FACE,{"disambiguationData":[OSD([subQ3,subQ2,subQ1,subQ0])]})],"blendedInto":[makeQuery(id+"F4.opExtrude","SWEPT_FACE",FACE,{"disambiguationData":[OSD([subQ3,subQ2,subQ1,subQ0])]})]});var subQ6=makeQuery(id+"F17.opChamfer","BLEND_EDGE",EDGE,{"blendedFrom":[makeQuery(id+"F15.opExtrude","CAP_EDGE",EDGE,{"disambiguationData":[OSD([subQ3,subQ2,subQ1,subQ0]),TDD([makeQuery(id+"F14.opChamfer","BLEND_EDGE",EDGE,{"blendedFrom":[makeQuery(id+"F13.opExtrude","CAP_EDGE",EDGE,{"disambiguationData":[OSD([subQ3,subQ2,subQ1,subQ0]),TDD([subQ5])],"isStart":false}),makeQuery(id+"F13.opExtrude","SWEPT_FACE",FACE,{"disambiguationData":[OSD([subQ3,subQ2,subQ1,subQ0]),TDD([subQ5])]})],"blendedInto":[makeQuery(id+"F13.opExtrude","SWEPT_FACE",FACE,{"disambiguationData":[OSD([subQ3,subQ2,subQ1,subQ0]),TDD([subQ5])]})]})])],"isStart":false}),makeQuery(id+"F15.opExtrude","CAP_FACE",FACE,{"disambiguationData":[OSD([subQ3,subQ2,subQ1,subQ0])],"isStart":false})],"blendedInto":[makeQuery(id+"F15.opExtrude","CAP_FACE",FACE,{"disambiguationData":[OSD([subQ3,subQ2,subQ1,subQ0])],"isStart":false})]});Q1=makeQuery(id+"F20.opChamfer","BLEND_EDGE",EDGE,{"blendedFrom":[makeQuery(id+"F18.boolean.opBoolean","MERGE",EDGE,{"derivedFrom":[subQ6,makeQuery(id+"F18.opExtrude","CAP_EDGE",EDGE,{"disambiguationData":[OSD([subQ3,subQ2,subQ1,subQ0]),TDD([subQ6])],"isStart":true})]}),makeQuery(id+"F19.boolean.opBoolean","MERGE",FACE,{"derivedFrom":[makeQuery(id+"F18.opExtrude","SWEPT_FACE",FACE,{"disambiguationData":[OSD([subQ3,subQ2,subQ1,subQ0]),TDD([subQ6])]}),makeQuery(id+"F19.opExtrude","SWEPT_FACE",FACE,{"disambiguationData":[OSD([subQ3,subQ2,subQ1,subQ0]),TDD([makeQuery(id+"F17.opChamfer","BLEND_EDGE",EDGE,{"blendedFrom":[makeQuery(id+"F16.opExtrude","CAP_EDGE",EDGE,{"disambiguationData":[OSD([subQ3,subQ2,subQ1,subQ0]),TDD([makeQuery(id+"F14.opChamfer","BLEND_EDGE",EDGE,{"blendedFrom":[makeQuery(id+"F12.opExtrude","CAP_EDGE",EDGE,{"disambiguationData":[OSD([subQ3,subQ2,subQ1,subQ0]),TDD([subQ4])],"isStart":false}),makeQuery(id+"F12.opExtrude","SWEPT_FACE",FACE,{"disambiguationData":[OSD([subQ3,subQ2,subQ1,subQ0]),TDD([subQ4])]})],"blendedInto":[makeQuery(id+"F12.opExtrude","SWEPT_FACE",FACE,{"disambiguationData":[OSD([subQ3,subQ2,subQ1,subQ0]),TDD([subQ4])]})]})])],"isStart":false}),makeQuery(id+"F16.opExtrude","CAP_FACE",FACE,{"disambiguationData":[OSD([subQ3,subQ2,subQ1,subQ0])],"isStart":false})],"blendedInto":[makeQuery(id+"F16.opExtrude","CAP_FACE",FACE,{"disambiguationData":[OSD([subQ3,subQ2,subQ1,subQ0])],"isStart":false})]})])]})]})],"blendedInto":[makeQuery(id+"F19.boolean.opBoolean","MERGE",FACE,{"derivedFrom":[makeQuery(id+"F18.opExtrude","SWEPT_FACE",FACE,{"disambiguationData":[OSD([subQ3,subQ2,subQ1,subQ0]),TDD([subQ6])]}),makeQuery(id+"F19.opExtrude","SWEPT_FACE",FACE,{"disambiguationData":[OSD([subQ3,subQ2,subQ1,subQ0]),TDD([makeQuery(id+"F17.opChamfer","BLEND_EDGE",EDGE,{"blendedFrom":[makeQuery(id+"F16.opExtrude","CAP_EDGE",EDGE,{"disambiguationData":[OSD([subQ3,subQ2,subQ1,subQ0]),TDD([makeQuery(id+"F14.opChamfer","BLEND_EDGE",EDGE,{"blendedFrom":[makeQuery(id+"F12.opExtrude","CAP_EDGE",EDGE,{"disambiguationData":[OSD([subQ3,subQ2,subQ1,subQ0]),TDD([subQ4])],"isStart":false}),makeQuery(id+"F12.opExtrude","SWEPT_FACE",FACE,{"disambiguationData":[OSD([subQ3,subQ2,subQ1,subQ0]),TDD([subQ4])]})],"blendedInto":[makeQuery(id+"F12.opExtrude","SWEPT_FACE",FACE,{"disambiguationData":[OSD([subQ3,subQ2,subQ1,subQ0]),TDD([subQ4])]})]})])],"isStart":false}),makeQuery(id+"F16.opExtrude","CAP_FACE",FACE,{"disambiguationData":[OSD([subQ3,subQ2,subQ1,subQ0])],"isStart":false})],"blendedInto":[makeQuery(id+"F16.opExtrude","CAP_FACE",FACE,{"disambiguationData":[OSD([subQ3,subQ2,subQ1,subQ0])],"isStart":false})]})])]})]})]});}
            chamfer(context, id + "F21", {"entities" : qUnion([Q0, Q1]), "width" : 5.08 * mm, "tangentPropagation" : true});
        }
        {
            var Q0;
            {var subQ0=sQuery(id+"F0.wireOp",EDGE,"E3");var subQ1=sQuery(id+"F0.wireOp",EDGE,"E2");var subQ2=sQuery(id+"F0.wireOp",EDGE,"E1");var subQ3=sQuery(id+"F0.wireOp",EDGE,"E0");var subQ4=makeQuery(id+"F9.opChamfer","BLEND_EDGE",EDGE,{"blendedFrom":[makeQuery(id+"F5.opExtrude","CAP_EDGE",EDGE,{"disambiguationData":[OSD([subQ3,subQ2,subQ1,subQ0])],"isStart":false}),makeQuery(id+"F5.opExtrude","SWEPT_FACE",FACE,{"disambiguationData":[OSD([subQ3,subQ2,subQ1,subQ0])]})],"blendedInto":[makeQuery(id+"F5.opExtrude","SWEPT_FACE",FACE,{"disambiguationData":[OSD([subQ3,subQ2,subQ1,subQ0])]})]});var subQ5=makeQuery(id+"F17.opChamfer","BLEND_EDGE",EDGE,{"blendedFrom":[makeQuery(id+"F16.opExtrude","CAP_EDGE",EDGE,{"disambiguationData":[OSD([subQ3,subQ2,subQ1,subQ0]),TDD([makeQuery(id+"F14.opChamfer","BLEND_EDGE",EDGE,{"blendedFrom":[makeQuery(id+"F12.opExtrude","CAP_EDGE",EDGE,{"disambiguationData":[OSD([subQ3,subQ2,subQ1,subQ0]),TDD([subQ4])],"isStart":false}),makeQuery(id+"F12.opExtrude","SWEPT_FACE",FACE,{"disambiguationData":[OSD([subQ3,subQ2,subQ1,subQ0]),TDD([subQ4])]})],"blendedInto":[makeQuery(id+"F12.opExtrude","SWEPT_FACE",FACE,{"disambiguationData":[OSD([subQ3,subQ2,subQ1,subQ0]),TDD([subQ4])]})]})])],"isStart":false}),makeQuery(id+"F16.opExtrude","CAP_FACE",FACE,{"disambiguationData":[OSD([subQ3,subQ2,subQ1,subQ0])],"isStart":false})],"blendedInto":[makeQuery(id+"F16.opExtrude","CAP_FACE",FACE,{"disambiguationData":[OSD([subQ3,subQ2,subQ1,subQ0])],"isStart":false})]});var subQ6=makeQuery(id+"F10.opChamfer","BLEND_EDGE",EDGE,{"blendedFrom":[makeQuery(id+"F4.opExtrude","CAP_EDGE",EDGE,{"disambiguationData":[OSD([subQ3,subQ2,subQ1,subQ0])],"isStart":false}),makeQuery(id+"F4.opExtrude","SWEPT_FACE",FACE,{"disambiguationData":[OSD([subQ3,subQ2,subQ1,subQ0])]})],"blendedInto":[makeQuery(id+"F4.opExtrude","SWEPT_FACE",FACE,{"disambiguationData":[OSD([subQ3,subQ2,subQ1,subQ0])]})]});var subQ7=makeQuery(id+"F19.boolean.opBoolean","MERGE",FACE,{"derivedFrom":[makeQuery(id+"F18.opExtrude","SWEPT_FACE",FACE,{"disambiguationData":[OSD([subQ3,subQ2,subQ1,subQ0]),TDD([makeQuery(id+"F17.opChamfer","BLEND_EDGE",EDGE,{"blendedFrom":[makeQuery(id+"F15.opExtrude","CAP_EDGE",EDGE,{"disambiguationData":[OSD([subQ3,subQ2,subQ1,subQ0]),TDD([makeQuery(id+"F14.opChamfer","BLEND_EDGE",EDGE,{"blendedFrom":[makeQuery(id+"F13.opExtrude","CAP_EDGE",EDGE,{"disambiguationData":[OSD([subQ3,subQ2,subQ1,subQ0]),TDD([subQ6])],"isStart":false}),makeQuery(id+"F13.opExtrude","SWEPT_FACE",FACE,{"disambiguationData":[OSD([subQ3,subQ2,subQ1,subQ0]),TDD([subQ6])]})],"blendedInto":[makeQuery(id+"F13.opExtrude","SWEPT_FACE",FACE,{"disambiguationData":[OSD([subQ3,subQ2,subQ1,subQ0]),TDD([subQ6])]})]})])],"isStart":false}),makeQuery(id+"F15.opExtrude","CAP_FACE",FACE,{"disambiguationData":[OSD([subQ3,subQ2,subQ1,subQ0])],"isStart":false})],"blendedInto":[makeQuery(id+"F15.opExtrude","CAP_FACE",FACE,{"disambiguationData":[OSD([subQ3,subQ2,subQ1,subQ0])],"isStart":false})]})])]}),makeQuery(id+"F19.opExtrude","SWEPT_FACE",FACE,{"disambiguationData":[OSD([subQ3,subQ2,subQ1,subQ0]),TDD([subQ5])]})]});Q0=makeQuery(id+"F21.opChamfer","BLEND_EDGE",EDGE,{"blendedFrom":[makeQuery(id+"F20.opChamfer","BLEND_EDGE",EDGE,{"blendedFrom":[makeQuery(id+"F19.boolean.opBoolean","MERGE",EDGE,{"derivedFrom":[subQ5,makeQuery(id+"F19.opExtrude","CAP_EDGE",EDGE,{"disambiguationData":[OSD([subQ3,subQ2,subQ1,subQ0]),TDD([subQ5])],"isStart":true})]}),subQ7],"blendedInto":[subQ7]}),subQ7],"blendedInto":[subQ7]});}
            var Q1;
            {var subQ0=sQuery(id+"F0.wireOp",EDGE,"E3");var subQ1=sQuery(id+"F0.wireOp",EDGE,"E2");var subQ2=sQuery(id+"F0.wireOp",EDGE,"E1");var subQ3=sQuery(id+"F0.wireOp",EDGE,"E0");var subQ4=makeQuery(id+"F9.opChamfer","BLEND_EDGE",EDGE,{"blendedFrom":[makeQuery(id+"F5.opExtrude","CAP_EDGE",EDGE,{"disambiguationData":[OSD([subQ3,subQ2,subQ1,subQ0])],"isStart":false}),makeQuery(id+"F5.opExtrude","SWEPT_FACE",FACE,{"disambiguationData":[OSD([subQ3,subQ2,subQ1,subQ0])]})],"blendedInto":[makeQuery(id+"F5.opExtrude","SWEPT_FACE",FACE,{"disambiguationData":[OSD([subQ3,subQ2,subQ1,subQ0])]})]});var subQ5=makeQuery(id+"F10.opChamfer","BLEND_EDGE",EDGE,{"blendedFrom":[makeQuery(id+"F4.opExtrude","CAP_EDGE",EDGE,{"disambiguationData":[OSD([subQ3,subQ2,subQ1,subQ0])],"isStart":false}),makeQuery(id+"F4.opExtrude","SWEPT_FACE",FACE,{"disambiguationData":[OSD([subQ3,subQ2,subQ1,subQ0])]})],"blendedInto":[makeQuery(id+"F4.opExtrude","SWEPT_FACE",FACE,{"disambiguationData":[OSD([subQ3,subQ2,subQ1,subQ0])]})]});var subQ6=makeQuery(id+"F17.opChamfer","BLEND_EDGE",EDGE,{"blendedFrom":[makeQuery(id+"F15.opExtrude","CAP_EDGE",EDGE,{"disambiguationData":[OSD([subQ3,subQ2,subQ1,subQ0]),TDD([makeQuery(id+"F14.opChamfer","BLEND_EDGE",EDGE,{"blendedFrom":[makeQuery(id+"F13.opExtrude","CAP_EDGE",EDGE,{"disambiguationData":[OSD([subQ3,subQ2,subQ1,subQ0]),TDD([subQ5])],"isStart":false}),makeQuery(id+"F13.opExtrude","SWEPT_FACE",FACE,{"disambiguationData":[OSD([subQ3,subQ2,subQ1,subQ0]),TDD([subQ5])]})],"blendedInto":[makeQuery(id+"F13.opExtrude","SWEPT_FACE",FACE,{"disambiguationData":[OSD([subQ3,subQ2,subQ1,subQ0]),TDD([subQ5])]})]})])],"isStart":false}),makeQuery(id+"F15.opExtrude","CAP_FACE",FACE,{"disambiguationData":[OSD([subQ3,subQ2,subQ1,subQ0])],"isStart":false})],"blendedInto":[makeQuery(id+"F15.opExtrude","CAP_FACE",FACE,{"disambiguationData":[OSD([subQ3,subQ2,subQ1,subQ0])],"isStart":false})]});var subQ7=makeQuery(id+"F19.boolean.opBoolean","MERGE",FACE,{"derivedFrom":[makeQuery(id+"F18.opExtrude","SWEPT_FACE",FACE,{"disambiguationData":[OSD([subQ3,subQ2,subQ1,subQ0]),TDD([subQ6])]}),makeQuery(id+"F19.opExtrude","SWEPT_FACE",FACE,{"disambiguationData":[OSD([subQ3,subQ2,subQ1,subQ0]),TDD([makeQuery(id+"F17.opChamfer","BLEND_EDGE",EDGE,{"blendedFrom":[makeQuery(id+"F16.opExtrude","CAP_EDGE",EDGE,{"disambiguationData":[OSD([subQ3,subQ2,subQ1,subQ0]),TDD([makeQuery(id+"F14.opChamfer","BLEND_EDGE",EDGE,{"blendedFrom":[makeQuery(id+"F12.opExtrude","CAP_EDGE",EDGE,{"disambiguationData":[OSD([subQ3,subQ2,subQ1,subQ0]),TDD([subQ4])],"isStart":false}),makeQuery(id+"F12.opExtrude","SWEPT_FACE",FACE,{"disambiguationData":[OSD([subQ3,subQ2,subQ1,subQ0]),TDD([subQ4])]})],"blendedInto":[makeQuery(id+"F12.opExtrude","SWEPT_FACE",FACE,{"disambiguationData":[OSD([subQ3,subQ2,subQ1,subQ0]),TDD([subQ4])]})]})])],"isStart":false}),makeQuery(id+"F16.opExtrude","CAP_FACE",FACE,{"disambiguationData":[OSD([subQ3,subQ2,subQ1,subQ0])],"isStart":false})],"blendedInto":[makeQuery(id+"F16.opExtrude","CAP_FACE",FACE,{"disambiguationData":[OSD([subQ3,subQ2,subQ1,subQ0])],"isStart":false})]})])]})]});Q1=makeQuery(id+"F21.opChamfer","BLEND_EDGE",EDGE,{"blendedFrom":[makeQuery(id+"F20.opChamfer","BLEND_EDGE",EDGE,{"blendedFrom":[makeQuery(id+"F18.boolean.opBoolean","MERGE",EDGE,{"derivedFrom":[subQ6,makeQuery(id+"F18.opExtrude","CAP_EDGE",EDGE,{"disambiguationData":[OSD([subQ3,subQ2,subQ1,subQ0]),TDD([subQ6])],"isStart":true})]}),subQ7],"blendedInto":[subQ7]}),subQ7],"blendedInto":[subQ7]});}
            chamfer(context, id + "F22", {"entities" : qUnion([Q0, Q1]), "width" : 5.08 * mm, "tangentPropagation" : true});
        }
        {
            var Q0;
            {var subQ0=sQuery(id+"F0.wireOp",EDGE,"E3");var subQ1=sQuery(id+"F0.wireOp",EDGE,"E2");var subQ2=sQuery(id+"F0.wireOp",EDGE,"E1");var subQ3=sQuery(id+"F0.wireOp",EDGE,"E0");var subQ4=makeQuery(id+"F9.opChamfer","BLEND_EDGE",EDGE,{"blendedFrom":[makeQuery(id+"F5.opExtrude","CAP_EDGE",EDGE,{"disambiguationData":[OSD([subQ3,subQ2,subQ1,subQ0])],"isStart":false}),makeQuery(id+"F5.opExtrude","SWEPT_FACE",FACE,{"disambiguationData":[OSD([subQ3,subQ2,subQ1,subQ0])]})],"blendedInto":[makeQuery(id+"F5.opExtrude","SWEPT_FACE",FACE,{"disambiguationData":[OSD([subQ3,subQ2,subQ1,subQ0])]})]});Q0=makeQuery(id+"F12.boolean.opBoolean","MERGE",EDGE,{"derivedFrom":[subQ4,makeQuery(id+"F12.opExtrude","CAP_EDGE",EDGE,{"disambiguationData":[OSD([subQ3,subQ2,subQ1,subQ0]),TDD([subQ4])],"isStart":true})]});}
            var Q1;
            {var subQ0=sQuery(id+"F0.wireOp",EDGE,"E3");var subQ1=sQuery(id+"F0.wireOp",EDGE,"E2");var subQ2=sQuery(id+"F0.wireOp",EDGE,"E1");var subQ3=sQuery(id+"F0.wireOp",EDGE,"E0");var subQ4=makeQuery(id+"F10.opChamfer","BLEND_EDGE",EDGE,{"blendedFrom":[makeQuery(id+"F4.opExtrude","CAP_EDGE",EDGE,{"disambiguationData":[OSD([subQ3,subQ2,subQ1,subQ0])],"isStart":false}),makeQuery(id+"F4.opExtrude","SWEPT_FACE",FACE,{"disambiguationData":[OSD([subQ3,subQ2,subQ1,subQ0])]})],"blendedInto":[makeQuery(id+"F4.opExtrude","SWEPT_FACE",FACE,{"disambiguationData":[OSD([subQ3,subQ2,subQ1,subQ0])]})]});Q1=makeQuery(id+"F13.boolean.opBoolean","MERGE",EDGE,{"derivedFrom":[subQ4,makeQuery(id+"F13.opExtrude","CAP_EDGE",EDGE,{"disambiguationData":[OSD([subQ3,subQ2,subQ1,subQ0]),TDD([subQ4])],"isStart":true})]});}
            var Q2;
            {var subQ0=sQuery(id+"F0.wireOp",EDGE,"E3");var subQ1=sQuery(id+"F0.wireOp",EDGE,"E2");var subQ2=sQuery(id+"F0.wireOp",EDGE,"E1");var subQ3=sQuery(id+"F0.wireOp",EDGE,"E0");var subQ4=makeQuery(id+"F10.opChamfer","BLEND_EDGE",EDGE,{"blendedFrom":[makeQuery(id+"F4.opExtrude","CAP_EDGE",EDGE,{"disambiguationData":[OSD([subQ3,subQ2,subQ1,subQ0])],"isStart":false}),makeQuery(id+"F4.opExtrude","SWEPT_FACE",FACE,{"disambiguationData":[OSD([subQ3,subQ2,subQ1,subQ0])]})],"blendedInto":[makeQuery(id+"F4.opExtrude","SWEPT_FACE",FACE,{"disambiguationData":[OSD([subQ3,subQ2,subQ1,subQ0])]})]});var subQ5=makeQuery(id+"F14.opChamfer","BLEND_EDGE",EDGE,{"blendedFrom":[makeQuery(id+"F13.opExtrude","CAP_EDGE",EDGE,{"disambiguationData":[OSD([subQ3,subQ2,subQ1,subQ0]),TDD([subQ4])],"isStart":false}),makeQuery(id+"F13.opExtrude","SWEPT_FACE",FACE,{"disambiguationData":[OSD([subQ3,subQ2,subQ1,subQ0]),TDD([subQ4])]})],"blendedInto":[makeQuery(id+"F13.opExtrude","SWEPT_FACE",FACE,{"disambiguationData":[OSD([subQ3,subQ2,subQ1,subQ0]),TDD([subQ4])]})]});Q2=makeQuery(id+"F15.boolean.opBoolean","MERGE",EDGE,{"derivedFrom":[subQ5,makeQuery(id+"F15.opExtrude","CAP_EDGE",EDGE,{"disambiguationData":[OSD([subQ3,subQ2,subQ1,subQ0]),TDD([subQ5])],"isStart":true})]});}
            var Q3;
            {var subQ0=sQuery(id+"F0.wireOp",EDGE,"E3");var subQ1=sQuery(id+"F0.wireOp",EDGE,"E2");var subQ2=sQuery(id+"F0.wireOp",EDGE,"E1");var subQ3=sQuery(id+"F0.wireOp",EDGE,"E0");var subQ4=makeQuery(id+"F10.opChamfer","BLEND_EDGE",EDGE,{"blendedFrom":[makeQuery(id+"F4.opExtrude","CAP_EDGE",EDGE,{"disambiguationData":[OSD([subQ3,subQ2,subQ1,subQ0])],"isStart":false}),makeQuery(id+"F4.opExtrude","SWEPT_FACE",FACE,{"disambiguationData":[OSD([subQ3,subQ2,subQ1,subQ0])]})],"blendedInto":[makeQuery(id+"F4.opExtrude","SWEPT_FACE",FACE,{"disambiguationData":[OSD([subQ3,subQ2,subQ1,subQ0])]})]});var subQ5=makeQuery(id+"F14.opChamfer","BLEND_EDGE",EDGE,{"blendedFrom":[makeQuery(id+"F13.opExtrude","CAP_EDGE",EDGE,{"disambiguationData":[OSD([subQ3,subQ2,subQ1,subQ0]),TDD([subQ4])],"isStart":false}),makeQuery(id+"F13.opExtrude","SWEPT_FACE",FACE,{"disambiguationData":[OSD([subQ3,subQ2,subQ1,subQ0]),TDD([subQ4])]})],"blendedInto":[makeQuery(id+"F13.opExtrude","SWEPT_FACE",FACE,{"disambiguationData":[OSD([subQ3,subQ2,subQ1,subQ0]),TDD([subQ4])]})]});var subQ6=makeQuery(id+"F17.opChamfer","BLEND_EDGE",EDGE,{"blendedFrom":[makeQuery(id+"F15.opExtrude","CAP_EDGE",EDGE,{"disambiguationData":[OSD([subQ3,subQ2,subQ1,subQ0]),TDD([subQ5])],"isStart":false}),makeQuery(id+"F15.opExtrude","SWEPT_FACE",FACE,{"disambiguationData":[OSD([subQ3,subQ2,subQ1,subQ0]),TDD([subQ5])]})],"blendedInto":[makeQuery(id+"F15.opExtrude","SWEPT_FACE",FACE,{"disambiguationData":[OSD([subQ3,subQ2,subQ1,subQ0]),TDD([subQ5])]})]});Q3=makeQuery(id+"F18.boolean.opBoolean","MERGE",EDGE,{"derivedFrom":[subQ6,makeQuery(id+"F18.opExtrude","CAP_EDGE",EDGE,{"disambiguationData":[OSD([subQ3,subQ2,subQ1,subQ0]),TDD([subQ6])],"isStart":true})]});}
            var Q4;
            {var subQ0=sQuery(id+"F0.wireOp",EDGE,"E3");var subQ1=sQuery(id+"F0.wireOp",EDGE,"E2");var subQ2=sQuery(id+"F0.wireOp",EDGE,"E1");var subQ3=sQuery(id+"F0.wireOp",EDGE,"E0");var subQ4=makeQuery(id+"F9.opChamfer","BLEND_EDGE",EDGE,{"blendedFrom":[makeQuery(id+"F5.opExtrude","CAP_EDGE",EDGE,{"disambiguationData":[OSD([subQ3,subQ2,subQ1,subQ0])],"isStart":false}),makeQuery(id+"F5.opExtrude","SWEPT_FACE",FACE,{"disambiguationData":[OSD([subQ3,subQ2,subQ1,subQ0])]})],"blendedInto":[makeQuery(id+"F5.opExtrude","SWEPT_FACE",FACE,{"disambiguationData":[OSD([subQ3,subQ2,subQ1,subQ0])]})]});var subQ5=makeQuery(id+"F14.opChamfer","BLEND_EDGE",EDGE,{"blendedFrom":[makeQuery(id+"F12.opExtrude","CAP_EDGE",EDGE,{"disambiguationData":[OSD([subQ3,subQ2,subQ1,subQ0]),TDD([subQ4])],"isStart":false}),makeQuery(id+"F12.opExtrude","SWEPT_FACE",FACE,{"disambiguationData":[OSD([subQ3,subQ2,subQ1,subQ0]),TDD([subQ4])]})],"blendedInto":[makeQuery(id+"F12.opExtrude","SWEPT_FACE",FACE,{"disambiguationData":[OSD([subQ3,subQ2,subQ1,subQ0]),TDD([subQ4])]})]});var subQ6=makeQuery(id+"F17.opChamfer","BLEND_EDGE",EDGE,{"blendedFrom":[makeQuery(id+"F16.opExtrude","CAP_EDGE",EDGE,{"disambiguationData":[OSD([subQ3,subQ2,subQ1,subQ0]),TDD([subQ5])],"isStart":false}),makeQuery(id+"F16.opExtrude","SWEPT_FACE",FACE,{"disambiguationData":[OSD([subQ3,subQ2,subQ1,subQ0]),TDD([subQ5])]})],"blendedInto":[makeQuery(id+"F16.opExtrude","SWEPT_FACE",FACE,{"disambiguationData":[OSD([subQ3,subQ2,subQ1,subQ0]),TDD([subQ5])]})]});Q4=makeQuery(id+"F19.boolean.opBoolean","MERGE",EDGE,{"derivedFrom":[subQ6,makeQuery(id+"F19.opExtrude","CAP_EDGE",EDGE,{"disambiguationData":[OSD([subQ3,subQ2,subQ1,subQ0]),TDD([subQ6])],"isStart":true})]});}
            var Q5;
            {var subQ0=sQuery(id+"F0.wireOp",EDGE,"E3");var subQ1=sQuery(id+"F0.wireOp",EDGE,"E2");var subQ2=sQuery(id+"F0.wireOp",EDGE,"E1");var subQ3=sQuery(id+"F0.wireOp",EDGE,"E0");var subQ4=makeQuery(id+"F9.opChamfer","BLEND_EDGE",EDGE,{"blendedFrom":[makeQuery(id+"F5.opExtrude","CAP_EDGE",EDGE,{"disambiguationData":[OSD([subQ3,subQ2,subQ1,subQ0])],"isStart":false}),makeQuery(id+"F5.opExtrude","SWEPT_FACE",FACE,{"disambiguationData":[OSD([subQ3,subQ2,subQ1,subQ0])]})],"blendedInto":[makeQuery(id+"F5.opExtrude","SWEPT_FACE",FACE,{"disambiguationData":[OSD([subQ3,subQ2,subQ1,subQ0])]})]});var subQ5=makeQuery(id+"F14.opChamfer","BLEND_EDGE",EDGE,{"blendedFrom":[makeQuery(id+"F12.opExtrude","CAP_EDGE",EDGE,{"disambiguationData":[OSD([subQ3,subQ2,subQ1,subQ0]),TDD([subQ4])],"isStart":false}),makeQuery(id+"F12.opExtrude","SWEPT_FACE",FACE,{"disambiguationData":[OSD([subQ3,subQ2,subQ1,subQ0]),TDD([subQ4])]})],"blendedInto":[makeQuery(id+"F12.opExtrude","SWEPT_FACE",FACE,{"disambiguationData":[OSD([subQ3,subQ2,subQ1,subQ0]),TDD([subQ4])]})]});Q5=makeQuery(id+"F16.boolean.opBoolean","MERGE",EDGE,{"derivedFrom":[subQ5,makeQuery(id+"F16.opExtrude","CAP_EDGE",EDGE,{"disambiguationData":[OSD([subQ3,subQ2,subQ1,subQ0]),TDD([subQ5])],"isStart":true})]});}
            chamfer(context, id + "F23", {"entities" : qUnion([Q0, Q1, Q2, Q3, Q4, Q5]), "width" : 5.08 * mm, "tangentPropagation" : true});
        }
        {
            var Q0;
            {var subQ0=sQuery(id+"F0.wireOp",EDGE,"E3");var subQ1=sQuery(id+"F0.wireOp",EDGE,"E2");var subQ2=sQuery(id+"F0.wireOp",EDGE,"E1");var subQ3=sQuery(id+"F0.wireOp",EDGE,"E0");var subQ4=makeQuery(id+"F14.opChamfer","BLEND_EDGE",EDGE,{"blendedFrom":[makeQuery(id+"F13.opExtrude","CAP_EDGE",EDGE,{"disambiguationData":[OSD([subQ3,subQ2,subQ1,subQ0]),TDD([makeQuery(id+"F10.opChamfer","BLEND_EDGE",EDGE,{"blendedFrom":[makeQuery(id+"F4.opExtrude","CAP_EDGE",EDGE,{"disambiguationData":[OSD([subQ3,subQ2,subQ1,subQ0])],"isStart":false}),makeQuery(id+"F4.opExtrude","SWEPT_FACE",FACE,{"disambiguationData":[OSD([subQ3,subQ2,subQ1,subQ0])]})],"blendedInto":[makeQuery(id+"F4.opExtrude","SWEPT_FACE",FACE,{"disambiguationData":[OSD([subQ3,subQ2,subQ1,subQ0])]})]})])],"isStart":false}),makeQuery(id+"F13.boolean.opBoolean","MERGE",FACE,{"derivedFrom":[makeQuery(id+"F11.opChamfer","BLEND_FACE",FACE,{"disambiguationData":[OSD([subQ0])]}),makeQuery(id+"F13.opExtrude","SWEPT_FACE",FACE,{"disambiguationData":[OSD([subQ3,subQ2,subQ1,subQ0]),TDD([makeQuery(id+"F11.opChamfer","BLEND_EDGE",EDGE,{"blendedFrom":[makeQuery(id+"F4.opExtrude","CAP_EDGE",EDGE,{"disambiguationData":[OSD([subQ0])],"isStart":false}),makeQuery(id+"F10.opChamfer","BLEND_FACE",FACE,{"disambiguationData":[OSD([subQ3,subQ2,subQ1,subQ0])]})],"blendedInto":[makeQuery(id+"F10.opChamfer","BLEND_FACE",FACE,{"disambiguationData":[OSD([subQ3,subQ2,subQ1,subQ0])]})]})])]})]})],"blendedInto":[makeQuery(id+"F13.boolean.opBoolean","MERGE",FACE,{"derivedFrom":[makeQuery(id+"F11.opChamfer","BLEND_FACE",FACE,{"disambiguationData":[OSD([subQ0])]}),makeQuery(id+"F13.opExtrude","SWEPT_FACE",FACE,{"disambiguationData":[OSD([subQ3,subQ2,subQ1,subQ0]),TDD([makeQuery(id+"F11.opChamfer","BLEND_EDGE",EDGE,{"blendedFrom":[makeQuery(id+"F4.opExtrude","CAP_EDGE",EDGE,{"disambiguationData":[OSD([subQ0])],"isStart":false}),makeQuery(id+"F10.opChamfer","BLEND_FACE",FACE,{"disambiguationData":[OSD([subQ3,subQ2,subQ1,subQ0])]})],"blendedInto":[makeQuery(id+"F10.opChamfer","BLEND_FACE",FACE,{"disambiguationData":[OSD([subQ3,subQ2,subQ1,subQ0])]})]})])]})]})]});Q0=makeQuery(id+"F15.boolean.opBoolean","MERGE",EDGE,{"derivedFrom":[subQ4,makeQuery(id+"F15.opExtrude","CAP_EDGE",EDGE,{"disambiguationData":[OSD([subQ3,subQ2,subQ1,subQ0]),TDD([subQ4])],"isStart":true})]});}
            var Q1;
            {var subQ0=sQuery(id+"F0.wireOp",EDGE,"E3");Q1=makeQuery(id+"F11.opChamfer","BLEND_EDGE",EDGE,{"blendedFrom":[makeQuery(id+"F4.opExtrude","CAP_EDGE",EDGE,{"disambiguationData":[OSD([subQ0])],"isStart":false}),makeQuery(id+"F4.opExtrude","SWEPT_FACE",FACE,{"disambiguationData":[OSD([subQ0])]})],"blendedInto":[makeQuery(id+"F4.opExtrude","SWEPT_FACE",FACE,{"disambiguationData":[OSD([subQ0])]})]});}
            var Q2;
            {var subQ0=sQuery(id+"F0.wireOp",EDGE,"E3");var subQ1=sQuery(id+"F0.wireOp",EDGE,"E2");var subQ2=sQuery(id+"F0.wireOp",EDGE,"E1");var subQ3=sQuery(id+"F0.wireOp",EDGE,"E0");var subQ4=makeQuery(id+"F14.opChamfer","BLEND_EDGE",EDGE,{"blendedFrom":[makeQuery(id+"F12.opExtrude","CAP_EDGE",EDGE,{"disambiguationData":[OSD([subQ3,subQ2,subQ1,subQ0]),TDD([makeQuery(id+"F9.opChamfer","BLEND_EDGE",EDGE,{"blendedFrom":[makeQuery(id+"F5.opExtrude","CAP_EDGE",EDGE,{"disambiguationData":[OSD([subQ3,subQ2,subQ1,subQ0])],"isStart":false}),makeQuery(id+"F5.opExtrude","SWEPT_FACE",FACE,{"disambiguationData":[OSD([subQ3,subQ2,subQ1,subQ0])]})],"blendedInto":[makeQuery(id+"F5.opExtrude","SWEPT_FACE",FACE,{"disambiguationData":[OSD([subQ3,subQ2,subQ1,subQ0])]})]})])],"isStart":false}),makeQuery(id+"F12.boolean.opBoolean","MERGE",FACE,{"derivedFrom":[makeQuery(id+"F10.opChamfer","BLEND_FACE",FACE,{"disambiguationData":[OSD([subQ2])]}),makeQuery(id+"F12.opExtrude","SWEPT_FACE",FACE,{"disambiguationData":[OSD([subQ3,subQ2,subQ1,subQ0]),TDD([makeQuery(id+"F10.opChamfer","BLEND_EDGE",EDGE,{"blendedFrom":[makeQuery(id+"F5.opExtrude","CAP_EDGE",EDGE,{"disambiguationData":[OSD([subQ2])],"isStart":false}),makeQuery(id+"F9.opChamfer","BLEND_FACE",FACE,{"disambiguationData":[OSD([subQ3,subQ2,subQ1,subQ0])]})],"blendedInto":[makeQuery(id+"F9.opChamfer","BLEND_FACE",FACE,{"disambiguationData":[OSD([subQ3,subQ2,subQ1,subQ0])]})]})])]})]})],"blendedInto":[makeQuery(id+"F12.boolean.opBoolean","MERGE",FACE,{"derivedFrom":[makeQuery(id+"F10.opChamfer","BLEND_FACE",FACE,{"disambiguationData":[OSD([subQ2])]}),makeQuery(id+"F12.opExtrude","SWEPT_FACE",FACE,{"disambiguationData":[OSD([subQ3,subQ2,subQ1,subQ0]),TDD([makeQuery(id+"F10.opChamfer","BLEND_EDGE",EDGE,{"blendedFrom":[makeQuery(id+"F5.opExtrude","CAP_EDGE",EDGE,{"disambiguationData":[OSD([subQ2])],"isStart":false}),makeQuery(id+"F9.opChamfer","BLEND_FACE",FACE,{"disambiguationData":[OSD([subQ3,subQ2,subQ1,subQ0])]})],"blendedInto":[makeQuery(id+"F9.opChamfer","BLEND_FACE",FACE,{"disambiguationData":[OSD([subQ3,subQ2,subQ1,subQ0])]})]})])]})]})]});Q2=makeQuery(id+"F16.boolean.opBoolean","MERGE",EDGE,{"derivedFrom":[subQ4,makeQuery(id+"F16.opExtrude","CAP_EDGE",EDGE,{"disambiguationData":[OSD([subQ3,subQ2,subQ1,subQ0]),TDD([subQ4])],"isStart":true})]});}
            var Q3;
            {var subQ0=sQuery(id+"F0.wireOp",EDGE,"E1");Q3=makeQuery(id+"F10.opChamfer","BLEND_EDGE",EDGE,{"blendedFrom":[makeQuery(id+"F5.opExtrude","CAP_EDGE",EDGE,{"disambiguationData":[OSD([subQ0])],"isStart":false}),makeQuery(id+"F5.opExtrude","SWEPT_FACE",FACE,{"disambiguationData":[OSD([subQ0])]})],"blendedInto":[makeQuery(id+"F5.opExtrude","SWEPT_FACE",FACE,{"disambiguationData":[OSD([subQ0])]})]});}
            chamfer(context, id + "F24", {"entities" : qUnion([Q0, Q1, Q2, Q3]), "width" : 5.08 * mm, "tangentPropagation" : true});
        }
        {
            var Q0;
            {var subQ0=sQuery(id+"F0.wireOp",EDGE,"E3");var subQ1=sQuery(id+"F0.wireOp",EDGE,"E2");var subQ2=sQuery(id+"F0.wireOp",EDGE,"E1");var subQ3=sQuery(id+"F0.wireOp",EDGE,"E0");var subQ4=makeQuery(id+"F14.opChamfer","BLEND_EDGE",EDGE,{"blendedFrom":[makeQuery(id+"F12.opExtrude","CAP_EDGE",EDGE,{"disambiguationData":[OSD([subQ3,subQ2,subQ1,subQ0]),TDD([makeQuery(id+"F9.opChamfer","BLEND_EDGE",EDGE,{"blendedFrom":[makeQuery(id+"F5.opExtrude","CAP_EDGE",EDGE,{"disambiguationData":[OSD([subQ3,subQ2,subQ1,subQ0])],"isStart":false}),makeQuery(id+"F5.opExtrude","SWEPT_FACE",FACE,{"disambiguationData":[OSD([subQ3,subQ2,subQ1,subQ0])]})],"blendedInto":[makeQuery(id+"F5.opExtrude","SWEPT_FACE",FACE,{"disambiguationData":[OSD([subQ3,subQ2,subQ1,subQ0])]})]})])],"isStart":false}),makeQuery(id+"F12.boolean.opBoolean","MERGE",FACE,{"derivedFrom":[makeQuery(id+"F10.opChamfer","BLEND_FACE",FACE,{"disambiguationData":[OSD([subQ2])]}),makeQuery(id+"F12.opExtrude","SWEPT_FACE",FACE,{"disambiguationData":[OSD([subQ3,subQ2,subQ1,subQ0]),TDD([makeQuery(id+"F10.opChamfer","BLEND_EDGE",EDGE,{"blendedFrom":[makeQuery(id+"F5.opExtrude","CAP_EDGE",EDGE,{"disambiguationData":[OSD([subQ2])],"isStart":false}),makeQuery(id+"F9.opChamfer","BLEND_FACE",FACE,{"disambiguationData":[OSD([subQ3,subQ2,subQ1,subQ0])]})],"blendedInto":[makeQuery(id+"F9.opChamfer","BLEND_FACE",FACE,{"disambiguationData":[OSD([subQ3,subQ2,subQ1,subQ0])]})]})])]})]})],"blendedInto":[makeQuery(id+"F12.boolean.opBoolean","MERGE",FACE,{"derivedFrom":[makeQuery(id+"F10.opChamfer","BLEND_FACE",FACE,{"disambiguationData":[OSD([subQ2])]}),makeQuery(id+"F12.opExtrude","SWEPT_FACE",FACE,{"disambiguationData":[OSD([subQ3,subQ2,subQ1,subQ0]),TDD([makeQuery(id+"F10.opChamfer","BLEND_EDGE",EDGE,{"blendedFrom":[makeQuery(id+"F5.opExtrude","CAP_EDGE",EDGE,{"disambiguationData":[OSD([subQ2])],"isStart":false}),makeQuery(id+"F9.opChamfer","BLEND_FACE",FACE,{"disambiguationData":[OSD([subQ3,subQ2,subQ1,subQ0])]})],"blendedInto":[makeQuery(id+"F9.opChamfer","BLEND_FACE",FACE,{"disambiguationData":[OSD([subQ3,subQ2,subQ1,subQ0])]})]})])]})]})]});Q0=makeQuery(id+"F24.opChamfer","BLEND_EDGE",EDGE,{"blendedFrom":[makeQuery(id+"F16.boolean.opBoolean","MERGE",EDGE,{"derivedFrom":[subQ4,makeQuery(id+"F16.opExtrude","CAP_EDGE",EDGE,{"disambiguationData":[OSD([subQ3,subQ2,subQ1,subQ0]),TDD([subQ4])],"isStart":true})]}),makeQuery(id+"F16.opExtrude","SWEPT_FACE",FACE,{"disambiguationData":[OSD([subQ3,subQ2,subQ1,subQ0]),TDD([subQ4])]})],"blendedInto":[makeQuery(id+"F16.opExtrude","SWEPT_FACE",FACE,{"disambiguationData":[OSD([subQ3,subQ2,subQ1,subQ0]),TDD([subQ4])]})]});}
            var Q1;
            {var subQ0=sQuery(id+"F0.wireOp",EDGE,"E3");var subQ1=sQuery(id+"F0.wireOp",EDGE,"E2");var subQ2=sQuery(id+"F0.wireOp",EDGE,"E1");var subQ3=sQuery(id+"F0.wireOp",EDGE,"E0");var subQ4=makeQuery(id+"F12.boolean.opBoolean","MERGE",FACE,{"derivedFrom":[makeQuery(id+"F10.opChamfer","BLEND_FACE",FACE,{"disambiguationData":[OSD([subQ2])]}),makeQuery(id+"F12.opExtrude","SWEPT_FACE",FACE,{"disambiguationData":[OSD([subQ3,subQ2,subQ1,subQ0]),TDD([makeQuery(id+"F10.opChamfer","BLEND_EDGE",EDGE,{"blendedFrom":[makeQuery(id+"F5.opExtrude","CAP_EDGE",EDGE,{"disambiguationData":[OSD([subQ2])],"isStart":false}),makeQuery(id+"F9.opChamfer","BLEND_FACE",FACE,{"disambiguationData":[OSD([subQ3,subQ2,subQ1,subQ0])]})],"blendedInto":[makeQuery(id+"F9.opChamfer","BLEND_FACE",FACE,{"disambiguationData":[OSD([subQ3,subQ2,subQ1,subQ0])]})]})])]})]});var subQ5=makeQuery(id+"F14.opChamfer","BLEND_EDGE",EDGE,{"blendedFrom":[makeQuery(id+"F12.opExtrude","CAP_EDGE",EDGE,{"disambiguationData":[OSD([subQ3,subQ2,subQ1,subQ0]),TDD([makeQuery(id+"F9.opChamfer","BLEND_EDGE",EDGE,{"blendedFrom":[makeQuery(id+"F5.opExtrude","CAP_EDGE",EDGE,{"disambiguationData":[OSD([subQ3,subQ2,subQ1,subQ0])],"isStart":false}),makeQuery(id+"F5.opExtrude","SWEPT_FACE",FACE,{"disambiguationData":[OSD([subQ3,subQ2,subQ1,subQ0])]})],"blendedInto":[makeQuery(id+"F5.opExtrude","SWEPT_FACE",FACE,{"disambiguationData":[OSD([subQ3,subQ2,subQ1,subQ0])]})]})])],"isStart":false}),subQ4],"blendedInto":[subQ4]});Q1=makeQuery(id+"F24.opChamfer","BLEND_EDGE",EDGE,{"blendedFrom":[makeQuery(id+"F16.boolean.opBoolean","MERGE",EDGE,{"derivedFrom":[subQ5,makeQuery(id+"F16.opExtrude","CAP_EDGE",EDGE,{"disambiguationData":[OSD([subQ3,subQ2,subQ1,subQ0]),TDD([subQ5])],"isStart":true})]}),subQ4],"blendedInto":[subQ4]});}
            var Q2;
            {var subQ0=sQuery(id+"F0.wireOp",EDGE,"E3");var subQ1=sQuery(id+"F0.wireOp",EDGE,"E2");var subQ2=sQuery(id+"F0.wireOp",EDGE,"E1");var subQ3=sQuery(id+"F0.wireOp",EDGE,"E0");var subQ4=makeQuery(id+"F5.opExtrude","CAP_EDGE",EDGE,{"disambiguationData":[OSD([subQ2])],"isStart":false});Q2=makeQuery(id+"F24.opChamfer","BLEND_EDGE",EDGE,{"blendedFrom":[makeQuery(id+"F10.opChamfer","BLEND_EDGE",EDGE,{"blendedFrom":[subQ4,makeQuery(id+"F5.opExtrude","SWEPT_FACE",FACE,{"disambiguationData":[OSD([subQ2])]})],"blendedInto":[makeQuery(id+"F5.opExtrude","SWEPT_FACE",FACE,{"disambiguationData":[OSD([subQ2])]})]}),makeQuery(id+"F12.boolean.opBoolean","MERGE",FACE,{"derivedFrom":[makeQuery(id+"F10.opChamfer","BLEND_FACE",FACE,{"disambiguationData":[OSD([subQ2])]}),makeQuery(id+"F12.opExtrude","SWEPT_FACE",FACE,{"disambiguationData":[OSD([subQ3,subQ2,subQ1,subQ0]),TDD([makeQuery(id+"F10.opChamfer","BLEND_EDGE",EDGE,{"blendedFrom":[subQ4,makeQuery(id+"F9.opChamfer","BLEND_FACE",FACE,{"disambiguationData":[OSD([subQ3,subQ2,subQ1,subQ0])]})],"blendedInto":[makeQuery(id+"F9.opChamfer","BLEND_FACE",FACE,{"disambiguationData":[OSD([subQ3,subQ2,subQ1,subQ0])]})]})])]})]})],"blendedInto":[makeQuery(id+"F12.boolean.opBoolean","MERGE",FACE,{"derivedFrom":[makeQuery(id+"F10.opChamfer","BLEND_FACE",FACE,{"disambiguationData":[OSD([subQ2])]}),makeQuery(id+"F12.opExtrude","SWEPT_FACE",FACE,{"disambiguationData":[OSD([subQ3,subQ2,subQ1,subQ0]),TDD([makeQuery(id+"F10.opChamfer","BLEND_EDGE",EDGE,{"blendedFrom":[subQ4,makeQuery(id+"F9.opChamfer","BLEND_FACE",FACE,{"disambiguationData":[OSD([subQ3,subQ2,subQ1,subQ0])]})],"blendedInto":[makeQuery(id+"F9.opChamfer","BLEND_FACE",FACE,{"disambiguationData":[OSD([subQ3,subQ2,subQ1,subQ0])]})]})])]})]})]});}
            var Q3;
            {var subQ0=sQuery(id+"F0.wireOp",EDGE,"E1");var subQ1=makeQuery(id+"F5.opExtrude","SWEPT_FACE",FACE,{"disambiguationData":[OSD([subQ0])]});Q3=makeQuery(id+"F24.opChamfer","BLEND_EDGE",EDGE,{"blendedFrom":[makeQuery(id+"F10.opChamfer","BLEND_EDGE",EDGE,{"blendedFrom":[makeQuery(id+"F5.opExtrude","CAP_EDGE",EDGE,{"disambiguationData":[OSD([subQ0])],"isStart":false}),subQ1],"blendedInto":[subQ1]}),subQ1],"blendedInto":[subQ1]});}
            var Q4;
            {var subQ0=sQuery(id+"F0.wireOp",EDGE,"E3");var subQ1=makeQuery(id+"F4.opExtrude","SWEPT_FACE",FACE,{"disambiguationData":[OSD([subQ0])]});Q4=makeQuery(id+"F24.opChamfer","BLEND_EDGE",EDGE,{"blendedFrom":[makeQuery(id+"F11.opChamfer","BLEND_EDGE",EDGE,{"blendedFrom":[makeQuery(id+"F4.opExtrude","CAP_EDGE",EDGE,{"disambiguationData":[OSD([subQ0])],"isStart":false}),subQ1],"blendedInto":[subQ1]}),subQ1],"blendedInto":[subQ1]});}
            var Q5;
            {var subQ0=sQuery(id+"F0.wireOp",EDGE,"E3");var subQ1=sQuery(id+"F0.wireOp",EDGE,"E2");var subQ2=sQuery(id+"F0.wireOp",EDGE,"E1");var subQ3=sQuery(id+"F0.wireOp",EDGE,"E0");var subQ4=makeQuery(id+"F4.opExtrude","CAP_EDGE",EDGE,{"disambiguationData":[OSD([subQ0])],"isStart":false});Q5=makeQuery(id+"F24.opChamfer","BLEND_EDGE",EDGE,{"blendedFrom":[makeQuery(id+"F11.opChamfer","BLEND_EDGE",EDGE,{"blendedFrom":[subQ4,makeQuery(id+"F4.opExtrude","SWEPT_FACE",FACE,{"disambiguationData":[OSD([subQ0])]})],"blendedInto":[makeQuery(id+"F4.opExtrude","SWEPT_FACE",FACE,{"disambiguationData":[OSD([subQ0])]})]}),makeQuery(id+"F13.boolean.opBoolean","MERGE",FACE,{"derivedFrom":[makeQuery(id+"F11.opChamfer","BLEND_FACE",FACE,{"disambiguationData":[OSD([subQ0])]}),makeQuery(id+"F13.opExtrude","SWEPT_FACE",FACE,{"disambiguationData":[OSD([subQ3,subQ2,subQ1,subQ0]),TDD([makeQuery(id+"F11.opChamfer","BLEND_EDGE",EDGE,{"blendedFrom":[subQ4,makeQuery(id+"F10.opChamfer","BLEND_FACE",FACE,{"disambiguationData":[OSD([subQ3,subQ2,subQ1,subQ0])]})],"blendedInto":[makeQuery(id+"F10.opChamfer","BLEND_FACE",FACE,{"disambiguationData":[OSD([subQ3,subQ2,subQ1,subQ0])]})]})])]})]})],"blendedInto":[makeQuery(id+"F13.boolean.opBoolean","MERGE",FACE,{"derivedFrom":[makeQuery(id+"F11.opChamfer","BLEND_FACE",FACE,{"disambiguationData":[OSD([subQ0])]}),makeQuery(id+"F13.opExtrude","SWEPT_FACE",FACE,{"disambiguationData":[OSD([subQ3,subQ2,subQ1,subQ0]),TDD([makeQuery(id+"F11.opChamfer","BLEND_EDGE",EDGE,{"blendedFrom":[subQ4,makeQuery(id+"F10.opChamfer","BLEND_FACE",FACE,{"disambiguationData":[OSD([subQ3,subQ2,subQ1,subQ0])]})],"blendedInto":[makeQuery(id+"F10.opChamfer","BLEND_FACE",FACE,{"disambiguationData":[OSD([subQ3,subQ2,subQ1,subQ0])]})]})])]})]})]});}
            var Q6;
            {var subQ0=sQuery(id+"F0.wireOp",EDGE,"E3");var subQ1=sQuery(id+"F0.wireOp",EDGE,"E2");var subQ2=sQuery(id+"F0.wireOp",EDGE,"E1");var subQ3=sQuery(id+"F0.wireOp",EDGE,"E0");var subQ4=makeQuery(id+"F13.boolean.opBoolean","MERGE",FACE,{"derivedFrom":[makeQuery(id+"F11.opChamfer","BLEND_FACE",FACE,{"disambiguationData":[OSD([subQ0])]}),makeQuery(id+"F13.opExtrude","SWEPT_FACE",FACE,{"disambiguationData":[OSD([subQ3,subQ2,subQ1,subQ0]),TDD([makeQuery(id+"F11.opChamfer","BLEND_EDGE",EDGE,{"blendedFrom":[makeQuery(id+"F4.opExtrude","CAP_EDGE",EDGE,{"disambiguationData":[OSD([subQ0])],"isStart":false}),makeQuery(id+"F10.opChamfer","BLEND_FACE",FACE,{"disambiguationData":[OSD([subQ3,subQ2,subQ1,subQ0])]})],"blendedInto":[makeQuery(id+"F10.opChamfer","BLEND_FACE",FACE,{"disambiguationData":[OSD([subQ3,subQ2,subQ1,subQ0])]})]})])]})]});var subQ5=makeQuery(id+"F14.opChamfer","BLEND_EDGE",EDGE,{"blendedFrom":[makeQuery(id+"F13.opExtrude","CAP_EDGE",EDGE,{"disambiguationData":[OSD([subQ3,subQ2,subQ1,subQ0]),TDD([makeQuery(id+"F10.opChamfer","BLEND_EDGE",EDGE,{"blendedFrom":[makeQuery(id+"F4.opExtrude","CAP_EDGE",EDGE,{"disambiguationData":[OSD([subQ3,subQ2,subQ1,subQ0])],"isStart":false}),makeQuery(id+"F4.opExtrude","SWEPT_FACE",FACE,{"disambiguationData":[OSD([subQ3,subQ2,subQ1,subQ0])]})],"blendedInto":[makeQuery(id+"F4.opExtrude","SWEPT_FACE",FACE,{"disambiguationData":[OSD([subQ3,subQ2,subQ1,subQ0])]})]})])],"isStart":false}),subQ4],"blendedInto":[subQ4]});Q6=makeQuery(id+"F24.opChamfer","BLEND_EDGE",EDGE,{"blendedFrom":[makeQuery(id+"F15.boolean.opBoolean","MERGE",EDGE,{"derivedFrom":[subQ5,makeQuery(id+"F15.opExtrude","CAP_EDGE",EDGE,{"disambiguationData":[OSD([subQ3,subQ2,subQ1,subQ0]),TDD([subQ5])],"isStart":true})]}),subQ4],"blendedInto":[subQ4]});}
            var Q7;
            {var subQ0=sQuery(id+"F0.wireOp",EDGE,"E3");var subQ1=sQuery(id+"F0.wireOp",EDGE,"E2");var subQ2=sQuery(id+"F0.wireOp",EDGE,"E1");var subQ3=sQuery(id+"F0.wireOp",EDGE,"E0");var subQ4=makeQuery(id+"F14.opChamfer","BLEND_EDGE",EDGE,{"blendedFrom":[makeQuery(id+"F13.opExtrude","CAP_EDGE",EDGE,{"disambiguationData":[OSD([subQ3,subQ2,subQ1,subQ0]),TDD([makeQuery(id+"F10.opChamfer","BLEND_EDGE",EDGE,{"blendedFrom":[makeQuery(id+"F4.opExtrude","CAP_EDGE",EDGE,{"disambiguationData":[OSD([subQ3,subQ2,subQ1,subQ0])],"isStart":false}),makeQuery(id+"F4.opExtrude","SWEPT_FACE",FACE,{"disambiguationData":[OSD([subQ3,subQ2,subQ1,subQ0])]})],"blendedInto":[makeQuery(id+"F4.opExtrude","SWEPT_FACE",FACE,{"disambiguationData":[OSD([subQ3,subQ2,subQ1,subQ0])]})]})])],"isStart":false}),makeQuery(id+"F13.boolean.opBoolean","MERGE",FACE,{"derivedFrom":[makeQuery(id+"F11.opChamfer","BLEND_FACE",FACE,{"disambiguationData":[OSD([subQ0])]}),makeQuery(id+"F13.opExtrude","SWEPT_FACE",FACE,{"disambiguationData":[OSD([subQ3,subQ2,subQ1,subQ0]),TDD([makeQuery(id+"F11.opChamfer","BLEND_EDGE",EDGE,{"blendedFrom":[makeQuery(id+"F4.opExtrude","CAP_EDGE",EDGE,{"disambiguationData":[OSD([subQ0])],"isStart":false}),makeQuery(id+"F10.opChamfer","BLEND_FACE",FACE,{"disambiguationData":[OSD([subQ3,subQ2,subQ1,subQ0])]})],"blendedInto":[makeQuery(id+"F10.opChamfer","BLEND_FACE",FACE,{"disambiguationData":[OSD([subQ3,subQ2,subQ1,subQ0])]})]})])]})]})],"blendedInto":[makeQuery(id+"F13.boolean.opBoolean","MERGE",FACE,{"derivedFrom":[makeQuery(id+"F11.opChamfer","BLEND_FACE",FACE,{"disambiguationData":[OSD([subQ0])]}),makeQuery(id+"F13.opExtrude","SWEPT_FACE",FACE,{"disambiguationData":[OSD([subQ3,subQ2,subQ1,subQ0]),TDD([makeQuery(id+"F11.opChamfer","BLEND_EDGE",EDGE,{"blendedFrom":[makeQuery(id+"F4.opExtrude","CAP_EDGE",EDGE,{"disambiguationData":[OSD([subQ0])],"isStart":false}),makeQuery(id+"F10.opChamfer","BLEND_FACE",FACE,{"disambiguationData":[OSD([subQ3,subQ2,subQ1,subQ0])]})],"blendedInto":[makeQuery(id+"F10.opChamfer","BLEND_FACE",FACE,{"disambiguationData":[OSD([subQ3,subQ2,subQ1,subQ0])]})]})])]})]})]});Q7=makeQuery(id+"F24.opChamfer","BLEND_EDGE",EDGE,{"blendedFrom":[makeQuery(id+"F15.boolean.opBoolean","MERGE",EDGE,{"derivedFrom":[subQ4,makeQuery(id+"F15.opExtrude","CAP_EDGE",EDGE,{"disambiguationData":[OSD([subQ3,subQ2,subQ1,subQ0]),TDD([subQ4])],"isStart":true})]}),makeQuery(id+"F15.opExtrude","SWEPT_FACE",FACE,{"disambiguationData":[OSD([subQ3,subQ2,subQ1,subQ0]),TDD([subQ4])]})],"blendedInto":[makeQuery(id+"F15.opExtrude","SWEPT_FACE",FACE,{"disambiguationData":[OSD([subQ3,subQ2,subQ1,subQ0]),TDD([subQ4])]})]});}
            chamfer(context, id + "F25", {"entities" : qUnion([Q0, Q1, Q2, Q3, Q4, Q5, Q6, Q7]), "width" : 5.08 * mm, "tangentPropagation" : true});
        }
        {
            var Q0;
            {var subQ0=sQuery(id+"F0.wireOp",EDGE,"E3");var subQ1=sQuery(id+"F0.wireOp",EDGE,"E2");var subQ2=sQuery(id+"F0.wireOp",EDGE,"E1");var subQ3=sQuery(id+"F0.wireOp",EDGE,"E0");var subQ4=makeQuery(id+"F1.opExtrude","CAP_FACE",FACE,{"disambiguationData":[OSD([subQ3,subQ2,subQ1,subQ0])],"isStart":false});Q0=makeQuery(id+"F8.opChamfer","BLEND_EDGE",EDGE,{"blendedFrom":[makeQuery(id+"F5.boolean.opBoolean","MERGE",EDGE,{"derivedFrom":[makeQuery(id+"F2.opChamfer","BLEND_EDGE",EDGE,{"blendedFrom":[makeQuery(id+"F1.opExtrude","CAP_EDGE",EDGE,{"disambiguationData":[OSD([subQ2])],"isStart":false}),subQ4],"blendedInto":[subQ4]}),makeQuery(id+"F5.opExtrude","CAP_EDGE",EDGE,{"disambiguationData":[OSD([subQ3,subQ2,subQ1,subQ0])],"isStart":true})]}),subQ4],"blendedInto":[subQ4]});}
            var Q1;
            {var subQ0=sQuery(id+"F0.wireOp",EDGE,"E3");var subQ1=sQuery(id+"F0.wireOp",EDGE,"E2");var subQ2=sQuery(id+"F0.wireOp",EDGE,"E1");var subQ3=sQuery(id+"F0.wireOp",EDGE,"E0");var subQ4=makeQuery(id+"F1.opExtrude","CAP_FACE",FACE,{"disambiguationData":[OSD([subQ3,subQ2,subQ1,subQ0])],"isStart":false});Q1=makeQuery(id+"F8.opChamfer","BLEND_EDGE",EDGE,{"blendedFrom":[makeQuery(id+"F4.boolean.opBoolean","MERGE",EDGE,{"derivedFrom":[makeQuery(id+"F2.opChamfer","BLEND_EDGE",EDGE,{"blendedFrom":[makeQuery(id+"F1.opExtrude","CAP_EDGE",EDGE,{"disambiguationData":[OSD([subQ0])],"isStart":false}),subQ4],"blendedInto":[subQ4]}),makeQuery(id+"F4.opExtrude","CAP_EDGE",EDGE,{"disambiguationData":[OSD([subQ3,subQ2,subQ1,subQ0])],"isStart":true})]}),subQ4],"blendedInto":[subQ4]});}
            chamfer(context, id + "F26", {"entities" : qUnion([Q0, Q1]), "width" : 5.08 * mm, "tangentPropagation" : true});
        }
        {
            var Q0;
            Q0=makeQuery(id+"F1.opExtrude","CAP_EDGE",EDGE,{"disambiguationData":[OSD([sQuery(id+"F0.wireOp",EDGE,"E2")])],"isStart":false});
            var Q1;
            Q1=makeQuery(id+"F1.opExtrude","CAP_EDGE",EDGE,{"disambiguationData":[OSD([sQuery(id+"F0.wireOp",EDGE,"E0")])],"isStart":false});
            fillet(context, id + "F27", {"entities" : qUnion([Q0, Q1]), "radius" : 5.08 * mm, "tangentPropagation" : true, "allowEdgeOverflow" : false});
        }
        {
            var Q0;
            Q0=makeQuery(id+"F1.opExtrude","SWEPT_FACE",FACE,{"disambiguationData":[OSD([sQuery(id+"F0.wireOp",EDGE,"E2")])]});
            var Q1;
            Q1=makeQuery(id+"F1.opExtrude","SWEPT_FACE",FACE,{"disambiguationData":[OSD([sQuery(id+"F0.wireOp",EDGE,"E0")])]});
            chamfer(context, id + "F28", {"entities" : qUnion([Q0, Q1]), "width" : 5.08 * mm, "tangentPropagation" : true});
        }
        {
            var Q0;
            {var subQ0=sQuery(id+"F0.wireOp",EDGE,"E1");Q0=makeQuery(id+"F5.boolean.opBoolean","MERGE",EDGE,{"derivedFrom":[makeQuery(id+"F2.opChamfer","BLEND_EDGE",EDGE,{"blendedFrom":[makeQuery(id+"F1.opExtrude","CAP_EDGE",EDGE,{"disambiguationData":[OSD([subQ0])],"isStart":false}),makeQuery(id+"F1.opExtrude","SWEPT_FACE",FACE,{"disambiguationData":[OSD([subQ0])]})],"blendedInto":[makeQuery(id+"F1.opExtrude","SWEPT_FACE",FACE,{"disambiguationData":[OSD([subQ0])]})]}),makeQuery(id+"F5.opExtrude","CAP_EDGE",EDGE,{"disambiguationData":[OSD([subQ0])],"isStart":true})]});}
            var Q1;
            {var subQ0=sQuery(id+"F0.wireOp",EDGE,"E3");Q1=makeQuery(id+"F4.boolean.opBoolean","MERGE",EDGE,{"derivedFrom":[makeQuery(id+"F2.opChamfer","BLEND_EDGE",EDGE,{"blendedFrom":[makeQuery(id+"F1.opExtrude","CAP_EDGE",EDGE,{"disambiguationData":[OSD([subQ0])],"isStart":false}),makeQuery(id+"F1.opExtrude","SWEPT_FACE",FACE,{"disambiguationData":[OSD([subQ0])]})],"blendedInto":[makeQuery(id+"F1.opExtrude","SWEPT_FACE",FACE,{"disambiguationData":[OSD([subQ0])]})]}),makeQuery(id+"F4.opExtrude","CAP_EDGE",EDGE,{"disambiguationData":[OSD([subQ0])],"isStart":true})]});}
            chamfer(context, id + "F29", {"entities" : qUnion([Q0, Q1]), "width" : 5.08 * mm, "tangentPropagation" : true});
        }
        {
            var Q0;
            {var subQ0=sQuery(id+"F0.wireOp",EDGE,"E3");var subQ1=makeQuery(id+"F1.opExtrude","SWEPT_FACE",FACE,{"disambiguationData":[OSD([subQ0])]});Q0=makeQuery(id+"F29.opChamfer","BLEND_EDGE",EDGE,{"blendedFrom":[makeQuery(id+"F4.boolean.opBoolean","MERGE",EDGE,{"derivedFrom":[makeQuery(id+"F2.opChamfer","BLEND_EDGE",EDGE,{"blendedFrom":[makeQuery(id+"F1.opExtrude","CAP_EDGE",EDGE,{"disambiguationData":[OSD([subQ0])],"isStart":false}),subQ1],"blendedInto":[subQ1]}),makeQuery(id+"F4.opExtrude","CAP_EDGE",EDGE,{"disambiguationData":[OSD([subQ0])],"isStart":true})]}),subQ1],"blendedInto":[subQ1]});}
            var Q1;
            {var subQ0=sQuery(id+"F0.wireOp",EDGE,"E1");var subQ1=makeQuery(id+"F1.opExtrude","SWEPT_FACE",FACE,{"disambiguationData":[OSD([subQ0])]});Q1=makeQuery(id+"F29.opChamfer","BLEND_EDGE",EDGE,{"blendedFrom":[makeQuery(id+"F5.boolean.opBoolean","MERGE",EDGE,{"derivedFrom":[makeQuery(id+"F2.opChamfer","BLEND_EDGE",EDGE,{"blendedFrom":[makeQuery(id+"F1.opExtrude","CAP_EDGE",EDGE,{"disambiguationData":[OSD([subQ0])],"isStart":false}),subQ1],"blendedInto":[subQ1]}),makeQuery(id+"F5.opExtrude","CAP_EDGE",EDGE,{"disambiguationData":[OSD([subQ0])],"isStart":true})]}),subQ1],"blendedInto":[subQ1]});}
            chamfer(context, id + "F30", {"entities" : qUnion([Q0, Q1]), "width" : 5.08 * mm, "tangentPropagation" : true});
        }
    });
